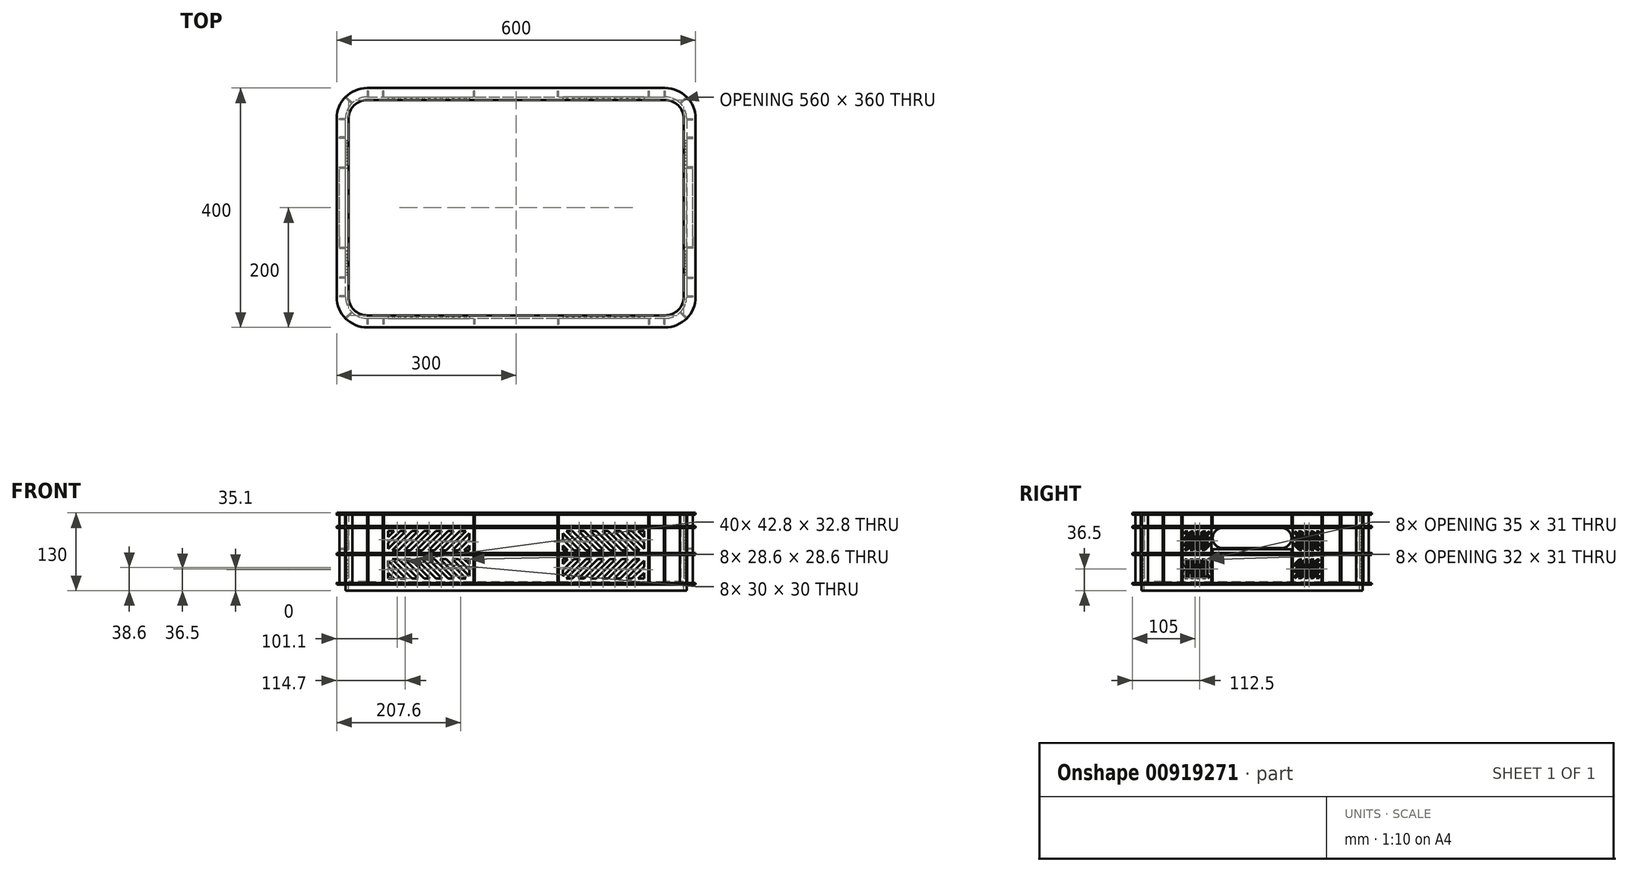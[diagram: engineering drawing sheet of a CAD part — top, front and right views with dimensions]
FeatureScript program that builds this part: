
annotation { "Feature Type Name" : "Feature", "Feature Type Description" : "" }
export const myFeature = defineFeature(function(context is Context, id is Id, definition is map)
    precondition{}
    {
        {
            var Q0;
            Q0=qCreatedBy(makeId("Top.planeOp"),FACE);
            var sketch = newSketch(context, id + "F0", { "sketchPlane" : qUnion([Q0])});
            skLineSegment(sketch, "E0.bottom", {"start": v(249, 185) * mm, "end": v(-249, 185) * mm});
            skLineSegment(sketch, "E0.top", {"start": v(249, -185) * mm, "end": v(-249, -185) * mm});
            skLineSegment(sketch, "E0.left", {"start": v(285, 149) * mm, "end": v(285, -149) * mm});
            skLineSegment(sketch, "E0.right", {"start": v(-285, 149) * mm, "end": v(-285, -149) * mm});
            skPoint(sketch, "E0.middle", {"position": v(0, 0) * mm});
            skPoint(sketch, "E1.visualSharp", {"position": v(-285, 185) * mm});
            skArc(sketch, "E1.filletArc", {"start": v(-249, 185) * mm, "mid": v(-274.46, 174.46) * mm, "end": v(-285, 149) * mm});
            skPoint(sketch, "E2.visualSharp", {"position": v(285, 185) * mm});
            skArc(sketch, "E2.filletArc", {"start": v(285, 149) * mm, "mid": v(274.46, 174.46) * mm, "end": v(249, 185) * mm});
            skPoint(sketch, "E3.visualSharp", {"position": v(285, -185) * mm});
            skArc(sketch, "E3.filletArc", {"start": v(249, -185) * mm, "mid": v(274.46, -174.46) * mm, "end": v(285, -149) * mm});
            skPoint(sketch, "E4.visualSharp", {"position": v(-285, -185) * mm});
            skArc(sketch, "E4.filletArc", {"start": v(-285, -149) * mm, "mid": v(-274.46, -174.46) * mm, "end": v(-249, -185) * mm});
            skSolve(sketch);
        }
        {
            var Q0;
            Q0 = qSketchRegion(id + "F0", true);
            extrude(context, id + "F1", {"entities" : qUnion([Q0]), "depth" : 120 * mm, "offsetDistance" : 25 * mm});
        }
        {
            var Q0;
            Q0=makeQuery(id+"F1.opExtrude","CAP_FACE",FACE,{"disambiguationData":[OSD([sQuery(id+"F0.wireOp",EDGE,"E0.bottom"),sQuery(id+"F0.wireOp",EDGE,"E0.top"),sQuery(id+"F0.wireOp",EDGE,"E0.left"),sQuery(id+"F0.wireOp",EDGE,"E0.right"),sQuery(id+"F0.wireOp",EDGE,"E1.filletArc"),sQuery(id+"F0.wireOp",EDGE,"E2.filletArc"),sQuery(id+"F0.wireOp",EDGE,"E3.filletArc"),sQuery(id+"F0.wireOp",EDGE,"E4.filletArc")])],"isStart":false});
            var sketch = newSketch(context, id + "F2", { "sketchPlane" : qUnion([Q0])});
            skArc(sketch, "E5.0", {"start": v(300, 149) * mm, "mid": v(285.06, 185.06) * mm, "end": v(249, 200) * mm});
            skLineSegment(sketch, "E5.1", {"start": v(300, 149) * mm, "end": v(300, -149) * mm});
            skLineSegment(sketch, "E5.2", {"start": v(249, 200) * mm, "end": v(-249, 200) * mm});
            skArc(sketch, "E5.3", {"start": v(249, -200) * mm, "mid": v(285.06, -185.06) * mm, "end": v(300, -149) * mm});
            skArc(sketch, "E5.4", {"start": v(-249, 200) * mm, "mid": v(-285.06, 185.06) * mm, "end": v(-300, 149) * mm});
            skLineSegment(sketch, "E5.5", {"start": v(-300, 149) * mm, "end": v(-300, -149) * mm});
            skArc(sketch, "E5.6", {"start": v(-300, -149) * mm, "mid": v(-285.06, -185.06) * mm, "end": v(-249, -200) * mm});
            skLineSegment(sketch, "E5.7", {"start": v(249, -200) * mm, "end": v(-249, -200) * mm});
            skSolve(sketch);
        }
        {
            var Q0;
            Q0 = qSketchRegion(id + "F2", true);
            extrude(context, id + "F3", {"entities" : qUnion([Q0]), "operationType" : NewBodyOperationType.ADD, "oppositeDirection" : true, "depth" : 3 * mm, "offsetDistance" : 25 * mm});
        }
        {
            var Q0;
            Q0=makeQuery(id+"F3.boolean.opBoolean","MERGE",FACE,{"derivedFrom":[makeQuery(id+"F1.opExtrude","CAP_FACE",FACE,{"disambiguationData":[OSD([sQuery(id+"F0.wireOp",EDGE,"E0.bottom"),sQuery(id+"F0.wireOp",EDGE,"E0.top"),sQuery(id+"F0.wireOp",EDGE,"E0.left"),sQuery(id+"F0.wireOp",EDGE,"E0.right"),sQuery(id+"F0.wireOp",EDGE,"E1.filletArc"),sQuery(id+"F0.wireOp",EDGE,"E2.filletArc"),sQuery(id+"F0.wireOp",EDGE,"E3.filletArc"),sQuery(id+"F0.wireOp",EDGE,"E4.filletArc")])],"isStart":false}),makeQuery(id+"F3.opExtrude","CAP_FACE",FACE,{"disambiguationData":[OSD([sQuery(id+"F2.wireOp",EDGE,"E5.0"),sQuery(id+"F2.wireOp",EDGE,"E5.1"),sQuery(id+"F2.wireOp",EDGE,"E5.2"),sQuery(id+"F2.wireOp",EDGE,"E5.3"),sQuery(id+"F2.wireOp",EDGE,"E5.4"),sQuery(id+"F2.wireOp",EDGE,"E5.5"),sQuery(id+"F2.wireOp",EDGE,"E5.6"),sQuery(id+"F2.wireOp",EDGE,"E5.7")])],"isStart":true})]});
            cPlane(context, id + "F4", {"entities" : qUnion([Q0]), "cplaneType" : CPlaneType.OFFSET, "offset" : 25 * mm, "oppositeDirection" : true, "width" : 150 * mm, "height" : 150 * mm});
        }
        {
            var Q0;
            Q0=qCreatedBy(id+"F4.planeOp",FACE);
            var sketch = newSketch(context, id + "F5", { "sketchPlane" : qUnion([Q0])});
            skLineSegment(sketch, "E6.0.0", {"start": v(249, -185) * mm, "end": v(-249, -185) * mm});
            skArc(sketch, "E6.0.1", {"start": v(-249, -185) * mm, "mid": v(-274.46, -174.46) * mm, "end": v(-285, -149) * mm});
            skLineSegment(sketch, "E6.0.2", {"start": v(-285, -149) * mm, "end": v(-285, 149) * mm});
            skArc(sketch, "E6.0.3", {"start": v(-285, 149) * mm, "mid": v(-274.46, 174.46) * mm, "end": v(-249, 185) * mm});
            skLineSegment(sketch, "E6.0.4", {"start": v(-249, 185) * mm, "end": v(249, 185) * mm});
            skArc(sketch, "E6.0.5", {"start": v(249, 185) * mm, "mid": v(274.46, 174.46) * mm, "end": v(285, 149) * mm});
            skLineSegment(sketch, "E6.0.6", {"start": v(285, 149) * mm, "end": v(285, -149) * mm});
            skArc(sketch, "E6.0.7", {"start": v(285, -149) * mm, "mid": v(274.46, -174.46) * mm, "end": v(249, -185) * mm});
            skLineSegment(sketch, "E7.0.0", {"start": v(249, -200) * mm, "end": v(-249, -200) * mm});
            skArc(sketch, "E7.0.1", {"start": v(-249, -200) * mm, "mid": v(-285.06, -185.06) * mm, "end": v(-300, -149) * mm});
            skLineSegment(sketch, "E7.0.2", {"start": v(-300, -149) * mm, "end": v(-300, 149) * mm});
            skArc(sketch, "E7.0.3", {"start": v(-300, 149) * mm, "mid": v(-285.06, 185.06) * mm, "end": v(-249, 200) * mm});
            skLineSegment(sketch, "E7.0.4", {"start": v(-249, 200) * mm, "end": v(249, 200) * mm});
            skArc(sketch, "E7.0.5", {"start": v(249, 200) * mm, "mid": v(285.06, 185.06) * mm, "end": v(300, 149) * mm});
            skLineSegment(sketch, "E7.0.6", {"start": v(300, 149) * mm, "end": v(300, -149) * mm});
            skArc(sketch, "E7.0.7", {"start": v(300, -149) * mm, "mid": v(285.06, -185.06) * mm, "end": v(249, -200) * mm});
            skSolve(sketch);
        }
        {
            var Q0;
            Q0 = qSketchRegion(id + "F5", true);
            extrude(context, id + "F6", {"entities" : qUnion([Q0]), "operationType" : NewBodyOperationType.ADD, "depth" : 3 * mm, "offsetDistance" : 25 * mm});
        }
        {
            var Q0;
            Q0=makeQuery(id+"F3.boolean.opBoolean","MERGE",FACE,{"derivedFrom":[makeQuery(id+"F1.opExtrude","CAP_FACE",FACE,{"disambiguationData":[OSD([sQuery(id+"F0.wireOp",EDGE,"E0.bottom"),sQuery(id+"F0.wireOp",EDGE,"E0.top"),sQuery(id+"F0.wireOp",EDGE,"E0.left"),sQuery(id+"F0.wireOp",EDGE,"E0.right"),sQuery(id+"F0.wireOp",EDGE,"E1.filletArc"),sQuery(id+"F0.wireOp",EDGE,"E2.filletArc"),sQuery(id+"F0.wireOp",EDGE,"E3.filletArc"),sQuery(id+"F0.wireOp",EDGE,"E4.filletArc")])],"isStart":false}),makeQuery(id+"F3.opExtrude","CAP_FACE",FACE,{"disambiguationData":[OSD([sQuery(id+"F2.wireOp",EDGE,"E5.0"),sQuery(id+"F2.wireOp",EDGE,"E5.1"),sQuery(id+"F2.wireOp",EDGE,"E5.2"),sQuery(id+"F2.wireOp",EDGE,"E5.3"),sQuery(id+"F2.wireOp",EDGE,"E5.4"),sQuery(id+"F2.wireOp",EDGE,"E5.5"),sQuery(id+"F2.wireOp",EDGE,"E5.6"),sQuery(id+"F2.wireOp",EDGE,"E5.7")])],"isStart":true})]});
            cPlane(context, id + "F7", {"entities" : qUnion([Q0]), "cplaneType" : CPlaneType.OFFSET, "offset" : 70 * mm, "oppositeDirection" : true, "width" : 150 * mm, "height" : 150 * mm});
        }
        {
            var Q0;
            Q0=qCreatedBy(id+"F7.planeOp",FACE);
            var sketch = newSketch(context, id + "F8", { "sketchPlane" : qUnion([Q0])});
            skLineSegment(sketch, "E8.0.0", {"start": v(249, -185) * mm, "end": v(-249, -185) * mm});
            skArc(sketch, "E8.0.1", {"start": v(-249, -185) * mm, "mid": v(-274.46, -174.46) * mm, "end": v(-285, -149) * mm});
            skLineSegment(sketch, "E8.0.2", {"start": v(-285, -149) * mm, "end": v(-285, 149) * mm});
            skArc(sketch, "E8.0.3", {"start": v(-285, 149) * mm, "mid": v(-274.46, 174.46) * mm, "end": v(-249, 185) * mm});
            skLineSegment(sketch, "E8.0.4", {"start": v(-249, 185) * mm, "end": v(249, 185) * mm});
            skArc(sketch, "E8.0.5", {"start": v(249, 185) * mm, "mid": v(274.46, 174.46) * mm, "end": v(285, 149) * mm});
            skLineSegment(sketch, "E8.0.6", {"start": v(285, 149) * mm, "end": v(285, -149) * mm});
            skArc(sketch, "E8.0.7", {"start": v(285, -149) * mm, "mid": v(274.46, -174.46) * mm, "end": v(249, -185) * mm});
            skArc(sketch, "E9.0.0", {"start": v(300, -149) * mm, "mid": v(285.06, -185.06) * mm, "end": v(249, -200) * mm});
            skLineSegment(sketch, "E9.0.1", {"start": v(249, -200) * mm, "end": v(-249, -200) * mm});
            skArc(sketch, "E9.0.2", {"start": v(-249, -200) * mm, "mid": v(-285.06, -185.06) * mm, "end": v(-300, -149) * mm});
            skLineSegment(sketch, "E9.0.3", {"start": v(-300, -149) * mm, "end": v(-300, 149) * mm});
            skArc(sketch, "E9.0.4", {"start": v(-300, 149) * mm, "mid": v(-285.06, 185.06) * mm, "end": v(-249, 200) * mm});
            skLineSegment(sketch, "E9.0.5", {"start": v(-249, 200) * mm, "end": v(249, 200) * mm});
            skArc(sketch, "E9.0.6", {"start": v(249, 200) * mm, "mid": v(285.06, 185.06) * mm, "end": v(300, 149) * mm});
            skLineSegment(sketch, "E9.0.7", {"start": v(300, 149) * mm, "end": v(300, -149) * mm});
            skSolve(sketch);
        }
        {
            var Q0;
            Q0 = qSketchRegion(id + "F8", true);
            extrude(context, id + "F9", {"entities" : qUnion([Q0]), "operationType" : NewBodyOperationType.ADD, "depth" : 3 * mm, "offsetDistance" : 25 * mm});
        }
        {
            var Q0;
            Q0=makeQuery(id+"F1.opExtrude","CAP_FACE",FACE,{"disambiguationData":[OSD([sQuery(id+"F0.wireOp",EDGE,"E0.bottom"),sQuery(id+"F0.wireOp",EDGE,"E0.top"),sQuery(id+"F0.wireOp",EDGE,"E0.left"),sQuery(id+"F0.wireOp",EDGE,"E0.right"),sQuery(id+"F0.wireOp",EDGE,"E1.filletArc"),sQuery(id+"F0.wireOp",EDGE,"E2.filletArc"),sQuery(id+"F0.wireOp",EDGE,"E3.filletArc"),sQuery(id+"F0.wireOp",EDGE,"E4.filletArc")])],"isStart":true});
            var sketch = newSketch(context, id + "F10", { "sketchPlane" : qUnion([Q0])});
            skLineSegment(sketch, "E10.0.0", {"start": v(249, 185) * mm, "end": v(-249, 185) * mm});
            skArc(sketch, "E10.0.1", {"start": v(-249, 185) * mm, "mid": v(-274.46, 174.46) * mm, "end": v(-285, 149) * mm});
            skLineSegment(sketch, "E10.0.2", {"start": v(-285, 149) * mm, "end": v(-285, -149) * mm});
            skArc(sketch, "E10.0.3", {"start": v(-285, -149) * mm, "mid": v(-274.46, -174.46) * mm, "end": v(-249, -185) * mm});
            skLineSegment(sketch, "E10.0.4", {"start": v(-249, -185) * mm, "end": v(249, -185) * mm});
            skArc(sketch, "E10.0.5", {"start": v(249, -185) * mm, "mid": v(274.46, -174.46) * mm, "end": v(285, -149) * mm});
            skLineSegment(sketch, "E10.0.6", {"start": v(285, -149) * mm, "end": v(285, 149) * mm});
            skArc(sketch, "E10.0.7", {"start": v(285, 149) * mm, "mid": v(274.46, 174.46) * mm, "end": v(249, 185) * mm});
            skLineSegment(sketch, "E11.0.0", {"start": v(300, -149) * mm, "end": v(300, 149) * mm});
            skArc(sketch, "E11.0.1", {"start": v(300, 149) * mm, "mid": v(285.06, 185.06) * mm, "end": v(249, 200) * mm});
            skLineSegment(sketch, "E11.0.2", {"start": v(249, 200) * mm, "end": v(-249, 200) * mm});
            skArc(sketch, "E11.0.3", {"start": v(-249, 200) * mm, "mid": v(-285.06, 185.06) * mm, "end": v(-300, 149) * mm});
            skLineSegment(sketch, "E11.0.4", {"start": v(-300, 149) * mm, "end": v(-300, -149) * mm});
            skArc(sketch, "E11.0.5", {"start": v(-300, -149) * mm, "mid": v(-285.06, -185.06) * mm, "end": v(-249, -200) * mm});
            skLineSegment(sketch, "E11.0.6", {"start": v(-249, -200) * mm, "end": v(249, -200) * mm});
            skArc(sketch, "E11.0.7", {"start": v(249, -200) * mm, "mid": v(285.06, -185.06) * mm, "end": v(300, -149) * mm});
            skSolve(sketch);
        }
        {
            var Q0;
            Q0 = qSketchRegion(id + "F10", true);
            extrude(context, id + "F11", {"entities" : qUnion([Q0]), "operationType" : NewBodyOperationType.ADD, "oppositeDirection" : true, "depth" : 3 * mm, "offsetDistance" : 25 * mm});
        }
        {
            var Q0;
            Q0=makeQuery(id+"F3.boolean.opBoolean","MERGE",FACE,{"derivedFrom":[makeQuery(id+"F1.opExtrude","CAP_FACE",FACE,{"disambiguationData":[OSD([sQuery(id+"F0.wireOp",EDGE,"E0.bottom"),sQuery(id+"F0.wireOp",EDGE,"E0.top"),sQuery(id+"F0.wireOp",EDGE,"E0.left"),sQuery(id+"F0.wireOp",EDGE,"E0.right"),sQuery(id+"F0.wireOp",EDGE,"E1.filletArc"),sQuery(id+"F0.wireOp",EDGE,"E2.filletArc"),sQuery(id+"F0.wireOp",EDGE,"E3.filletArc"),sQuery(id+"F0.wireOp",EDGE,"E4.filletArc")])],"isStart":false}),makeQuery(id+"F3.opExtrude","CAP_FACE",FACE,{"disambiguationData":[OSD([sQuery(id+"F2.wireOp",EDGE,"E5.0"),sQuery(id+"F2.wireOp",EDGE,"E5.1"),sQuery(id+"F2.wireOp",EDGE,"E5.2"),sQuery(id+"F2.wireOp",EDGE,"E5.3"),sQuery(id+"F2.wireOp",EDGE,"E5.4"),sQuery(id+"F2.wireOp",EDGE,"E5.5"),sQuery(id+"F2.wireOp",EDGE,"E5.6"),sQuery(id+"F2.wireOp",EDGE,"E5.7")])],"isStart":true})]});
            shell(context, id + "F12", {"entities" : qUnion([Q0]), "thickness" : 5 * mm});
        }
        {
            var Q0;
            Q0=makeQuery(id+"F11.boolean.opBoolean","MERGE",FACE,{"derivedFrom":[makeQuery(id+"F1.opExtrude","CAP_FACE",FACE,{"disambiguationData":[OSD([sQuery(id+"F0.wireOp",EDGE,"E0.bottom"),sQuery(id+"F0.wireOp",EDGE,"E0.top"),sQuery(id+"F0.wireOp",EDGE,"E0.left"),sQuery(id+"F0.wireOp",EDGE,"E0.right"),sQuery(id+"F0.wireOp",EDGE,"E1.filletArc"),sQuery(id+"F0.wireOp",EDGE,"E2.filletArc"),sQuery(id+"F0.wireOp",EDGE,"E3.filletArc"),sQuery(id+"F0.wireOp",EDGE,"E4.filletArc")])],"isStart":true}),makeQuery(id+"F11.opExtrude","CAP_FACE",FACE,{"disambiguationData":[OSD([sQuery(id+"F10.wireOp",EDGE,"E10.0.0"),sQuery(id+"F10.wireOp",EDGE,"E10.0.1"),sQuery(id+"F10.wireOp",EDGE,"E10.0.2"),sQuery(id+"F10.wireOp",EDGE,"E10.0.3"),sQuery(id+"F10.wireOp",EDGE,"E10.0.4"),sQuery(id+"F10.wireOp",EDGE,"E10.0.5"),sQuery(id+"F10.wireOp",EDGE,"E10.0.6"),sQuery(id+"F10.wireOp",EDGE,"E10.0.7"),sQuery(id+"F10.wireOp",EDGE,"E11.0.0"),sQuery(id+"F10.wireOp",EDGE,"E11.0.1"),sQuery(id+"F10.wireOp",EDGE,"E11.0.2"),sQuery(id+"F10.wireOp",EDGE,"E11.0.3"),sQuery(id+"F10.wireOp",EDGE,"E11.0.4"),sQuery(id+"F10.wireOp",EDGE,"E11.0.5"),sQuery(id+"F10.wireOp",EDGE,"E11.0.6"),sQuery(id+"F10.wireOp",EDGE,"E11.0.7")])],"isStart":true})]});
            var sketch = newSketch(context, id + "F13", { "sketchPlane" : qUnion([Q0])});
            skLineSegment(sketch, "E12.0", {"start": v(249, 185) * mm, "end": v(-249, 185) * mm});
            skArc(sketch, "E12.1", {"start": v(285, 149) * mm, "mid": v(274.46, 174.46) * mm, "end": v(249, 185) * mm});
            skArc(sketch, "E12.2", {"start": v(-249, 185) * mm, "mid": v(-274.46, 174.46) * mm, "end": v(-285, 149) * mm});
            skLineSegment(sketch, "E12.3", {"start": v(285, -149) * mm, "end": v(285, 149) * mm});
            skLineSegment(sketch, "E12.4", {"start": v(-285, 149) * mm, "end": v(-285, -149) * mm});
            skArc(sketch, "E12.5", {"start": v(-285, -149) * mm, "mid": v(-274.46, -174.46) * mm, "end": v(-249, -185) * mm});
            skLineSegment(sketch, "E12.6", {"start": v(-249, -185) * mm, "end": v(249, -185) * mm});
            skArc(sketch, "E12.7", {"start": v(249, -185) * mm, "mid": v(274.46, -174.46) * mm, "end": v(285, -149) * mm});
            skArc(sketch, "E13.0", {"start": v(280, 149) * mm, "mid": v(270.92, 170.92) * mm, "end": v(249, 180) * mm});
            skLineSegment(sketch, "E13.1", {"start": v(280, -149) * mm, "end": v(280, 149) * mm});
            skLineSegment(sketch, "E13.2", {"start": v(249, 180) * mm, "end": v(-249, 180) * mm});
            skArc(sketch, "E13.3", {"start": v(249, -180) * mm, "mid": v(270.92, -170.92) * mm, "end": v(280, -149) * mm});
            skArc(sketch, "E13.4", {"start": v(-249, 180) * mm, "mid": v(-270.92, 170.92) * mm, "end": v(-280, 149) * mm});
            skLineSegment(sketch, "E13.5", {"start": v(-280, 149) * mm, "end": v(-280, -149) * mm});
            skArc(sketch, "E13.6", {"start": v(-280, -149) * mm, "mid": v(-270.92, -170.92) * mm, "end": v(-249, -180) * mm});
            skLineSegment(sketch, "E13.7", {"start": v(-249, -180) * mm, "end": v(249, -180) * mm});
            skSolve(sketch);
        }
        {
            var Q0;
            Q0 = qSketchRegion(id + "F13", true);
            extrude(context, id + "F14", {"entities" : qUnion([Q0]), "operationType" : NewBodyOperationType.ADD, "depth" : 10 * mm, "offsetDistance" : 25 * mm});
        }
        {
            var Q0;
            Q0=makeQuery(id+"F14.boolean.opBoolean","SPLIT",FACE,{"disambiguationData":[TD([makeQuery(id+"F14.opExtrude","SWEPT_FACE",FACE,{"disambiguationData":[OSD([sQuery(id+"F13.wireOp",EDGE,"E13.0")])]})])],"derivedFrom":makeQuery(id+"F11.boolean.opBoolean","MERGE",FACE,{"derivedFrom":[makeQuery(id+"F1.opExtrude","CAP_FACE",FACE,{"disambiguationData":[OSD([sQuery(id+"F0.wireOp",EDGE,"E0.bottom"),sQuery(id+"F0.wireOp",EDGE,"E0.top"),sQuery(id+"F0.wireOp",EDGE,"E0.left"),sQuery(id+"F0.wireOp",EDGE,"E0.right"),sQuery(id+"F0.wireOp",EDGE,"E1.filletArc"),sQuery(id+"F0.wireOp",EDGE,"E2.filletArc"),sQuery(id+"F0.wireOp",EDGE,"E3.filletArc"),sQuery(id+"F0.wireOp",EDGE,"E4.filletArc")])],"isStart":true}),makeQuery(id+"F11.opExtrude","CAP_FACE",FACE,{"disambiguationData":[OSD([sQuery(id+"F10.wireOp",EDGE,"E10.0.0"),sQuery(id+"F10.wireOp",EDGE,"E10.0.1"),sQuery(id+"F10.wireOp",EDGE,"E10.0.2"),sQuery(id+"F10.wireOp",EDGE,"E10.0.3"),sQuery(id+"F10.wireOp",EDGE,"E10.0.4"),sQuery(id+"F10.wireOp",EDGE,"E10.0.5"),sQuery(id+"F10.wireOp",EDGE,"E10.0.6"),sQuery(id+"F10.wireOp",EDGE,"E10.0.7"),sQuery(id+"F10.wireOp",EDGE,"E11.0.0"),sQuery(id+"F10.wireOp",EDGE,"E11.0.1"),sQuery(id+"F10.wireOp",EDGE,"E11.0.2"),sQuery(id+"F10.wireOp",EDGE,"E11.0.3"),sQuery(id+"F10.wireOp",EDGE,"E11.0.4"),sQuery(id+"F10.wireOp",EDGE,"E11.0.5"),sQuery(id+"F10.wireOp",EDGE,"E11.0.6"),sQuery(id+"F10.wireOp",EDGE,"E11.0.7")])],"isStart":true})]})});
            var sketch = newSketch(context, id + "F15", { "sketchPlane" : qUnion([Q0])});
            skLineSegment(sketch, "E14.bottom", {"start": v(-249, 185) * mm, "end": v(-247, 185) * mm});
            skLineSegment(sketch, "E14.top", {"start": v(-249, 195) * mm, "end": v(-247, 195) * mm});
            skLineSegment(sketch, "E14.left", {"start": v(-249, 185) * mm, "end": v(-249, 195) * mm});
            skLineSegment(sketch, "E14.right", {"start": v(-247, 185) * mm, "end": v(-247, 195) * mm});
            skLineSegment(sketch, "E15.bottom", {"start": v(-71, 195) * mm, "end": v(-69, 195) * mm});
            skLineSegment(sketch, "E15.top", {"start": v(-71, 185) * mm, "end": v(-69, 185) * mm});
            skLineSegment(sketch, "E15.left", {"start": v(-71, 195) * mm, "end": v(-71, 185) * mm});
            skLineSegment(sketch, "E15.right", {"start": v(-69, 195) * mm, "end": v(-69, 185) * mm});
            skLineSegment(sketch, "E16.bottom", {"start": v(-223, 195) * mm, "end": v(-221, 195) * mm});
            skLineSegment(sketch, "E16.top", {"start": v(-223, 185) * mm, "end": v(-221, 185) * mm});
            skLineSegment(sketch, "E16.left", {"start": v(-223, 195) * mm, "end": v(-223, 185) * mm});
            skLineSegment(sketch, "E16.right", {"start": v(-221, 195) * mm, "end": v(-221, 185) * mm});
            skLineSegment(sketch, "E17.bottom", {"start": v(-285, 68) * mm, "end": v(-295, 68) * mm});
            skLineSegment(sketch, "E17.top", {"start": v(-285, 66) * mm, "end": v(-295, 66) * mm});
            skLineSegment(sketch, "E17.left", {"start": v(-285, 68) * mm, "end": v(-285, 66) * mm});
            skLineSegment(sketch, "E17.right", {"start": v(-295, 68) * mm, "end": v(-295, 66) * mm});
            skLineSegment(sketch, "E18.bottom", {"start": v(-295, 149) * mm, "end": v(-285, 149) * mm});
            skLineSegment(sketch, "E18.top", {"start": v(-295, 147) * mm, "end": v(-285, 147) * mm});
            skLineSegment(sketch, "E18.left", {"start": v(-295, 149) * mm, "end": v(-295, 147) * mm});
            skLineSegment(sketch, "E18.right", {"start": v(-285, 149) * mm, "end": v(-285, 147) * mm});
            skLineSegment(sketch, "E19.bottom", {"start": v(-295, 118) * mm, "end": v(-285, 118) * mm});
            skLineSegment(sketch, "E19.top", {"start": v(-295, 116) * mm, "end": v(-285, 116) * mm});
            skLineSegment(sketch, "E19.left", {"start": v(-295, 118) * mm, "end": v(-295, 116) * mm});
            skLineSegment(sketch, "E19.right", {"start": v(-285, 118) * mm, "end": v(-285, 116) * mm});
            skSolve(sketch);
        }
        {
            var Q0;
            Q0 = qSketchRegion(id + "F15", true);
            var Q1;
            Q1=makeQuery(id+"F3.opExtrude","CAP_FACE",FACE,{"disambiguationData":[OSD([sQuery(id+"F2.wireOp",EDGE,"E5.0"),sQuery(id+"F2.wireOp",EDGE,"E5.1"),sQuery(id+"F2.wireOp",EDGE,"E5.2"),sQuery(id+"F2.wireOp",EDGE,"E5.3"),sQuery(id+"F2.wireOp",EDGE,"E5.4"),sQuery(id+"F2.wireOp",EDGE,"E5.5"),sQuery(id+"F2.wireOp",EDGE,"E5.6"),sQuery(id+"F2.wireOp",EDGE,"E5.7")])],"isStart":false});
            extrude(context, id + "F16", {"entities" : qUnion([Q0]), "operationType" : NewBodyOperationType.ADD, "endBound" : BoundingType.UP_TO_SURFACE, "oppositeDirection" : true, "depth" : 25 * mm, "endBoundEntityFace" : qUnion([Q1]), "offsetDistance" : 25 * mm});
        }
        {
            var Q0;
            Q0=makeQuery(id+"F14.boolean.opBoolean","SPLIT",FACE,{"disambiguationData":[TD([makeQuery(id+"F14.opExtrude","SWEPT_FACE",FACE,{"disambiguationData":[OSD([sQuery(id+"F13.wireOp",EDGE,"E13.0")])]})])],"derivedFrom":makeQuery(id+"F11.boolean.opBoolean","MERGE",FACE,{"derivedFrom":[makeQuery(id+"F1.opExtrude","CAP_FACE",FACE,{"disambiguationData":[OSD([sQuery(id+"F0.wireOp",EDGE,"E0.bottom"),sQuery(id+"F0.wireOp",EDGE,"E0.top"),sQuery(id+"F0.wireOp",EDGE,"E0.left"),sQuery(id+"F0.wireOp",EDGE,"E0.right"),sQuery(id+"F0.wireOp",EDGE,"E1.filletArc"),sQuery(id+"F0.wireOp",EDGE,"E2.filletArc"),sQuery(id+"F0.wireOp",EDGE,"E3.filletArc"),sQuery(id+"F0.wireOp",EDGE,"E4.filletArc")])],"isStart":true}),makeQuery(id+"F11.opExtrude","CAP_FACE",FACE,{"disambiguationData":[OSD([sQuery(id+"F10.wireOp",EDGE,"E10.0.0"),sQuery(id+"F10.wireOp",EDGE,"E10.0.1"),sQuery(id+"F10.wireOp",EDGE,"E10.0.2"),sQuery(id+"F10.wireOp",EDGE,"E10.0.3"),sQuery(id+"F10.wireOp",EDGE,"E10.0.4"),sQuery(id+"F10.wireOp",EDGE,"E10.0.5"),sQuery(id+"F10.wireOp",EDGE,"E10.0.6"),sQuery(id+"F10.wireOp",EDGE,"E10.0.7"),sQuery(id+"F10.wireOp",EDGE,"E11.0.0"),sQuery(id+"F10.wireOp",EDGE,"E11.0.1"),sQuery(id+"F10.wireOp",EDGE,"E11.0.2"),sQuery(id+"F10.wireOp",EDGE,"E11.0.3"),sQuery(id+"F10.wireOp",EDGE,"E11.0.4"),sQuery(id+"F10.wireOp",EDGE,"E11.0.5"),sQuery(id+"F10.wireOp",EDGE,"E11.0.6"),sQuery(id+"F10.wireOp",EDGE,"E11.0.7")])],"isStart":true})]})});
            var sketch = newSketch(context, id + "F17", { "sketchPlane" : qUnion([Q0])});
            skLineSegment(sketch, "E20", {"start": v(-285.06, 185.06) * mm, "end": v(-270.92, 170.92) * mm, "construction": true});
            skArc(sketch, "E21.0", {"start": v(-273.74, 175.15) * mm, "mid": v(-274.46, 174.46) * mm, "end": v(-275.15, 173.74) * mm});
            skArc(sketch, "E22.0", {"start": v(-284.35, 185.76) * mm, "mid": v(-285.06, 185.06) * mm, "end": v(-285.76, 184.35) * mm});
            skLineSegment(sketch, "E23.0", {"start": v(-285.76, 184.35) * mm, "end": v(-275.15, 173.74) * mm});
            skLineSegment(sketch, "E24.0", {"start": v(-284.35, 185.76) * mm, "end": v(-273.74, 175.15) * mm});
            skPoint(sketch, "E25.orphan", {"position": v(-249, 185) * mm});
            skPoint(sketch, "E26.orphan", {"position": v(-249, 200) * mm});
            skPoint(sketch, "E27.orphan", {"position": v(-300, 149) * mm});
            skPoint(sketch, "E28.orphan", {"position": v(-285, 149) * mm});
            skSolve(sketch);
        }
        {
            var Q0;
            Q0 = qSketchRegion(id + "F17", true);
            var Q1;
            Q1=makeQuery(id+"F3.opExtrude","CAP_FACE",FACE,{"disambiguationData":[OSD([sQuery(id+"F2.wireOp",EDGE,"E5.0"),sQuery(id+"F2.wireOp",EDGE,"E5.1"),sQuery(id+"F2.wireOp",EDGE,"E5.2"),sQuery(id+"F2.wireOp",EDGE,"E5.3"),sQuery(id+"F2.wireOp",EDGE,"E5.4"),sQuery(id+"F2.wireOp",EDGE,"E5.5"),sQuery(id+"F2.wireOp",EDGE,"E5.6"),sQuery(id+"F2.wireOp",EDGE,"E5.7")])],"isStart":false});
            extrude(context, id + "F18", {"entities" : qUnion([Q0]), "operationType" : NewBodyOperationType.ADD, "endBound" : BoundingType.UP_TO_SURFACE, "oppositeDirection" : true, "depth" : 25 * mm, "endBoundEntityFace" : qUnion([Q1]), "offsetDistance" : 25 * mm});
        }
        {
            var Q0;
            Q0=makeQuery(id+"F1.opExtrude","SWEPT_BODY",BODY,{"disambiguationData":[OSD([sQuery(id+"F0.wireOp",EDGE,"E0.bottom"),sQuery(id+"F0.wireOp",EDGE,"E0.top"),sQuery(id+"F0.wireOp",EDGE,"E0.left"),sQuery(id+"F0.wireOp",EDGE,"E0.right"),sQuery(id+"F0.wireOp",EDGE,"E1.filletArc"),sQuery(id+"F0.wireOp",EDGE,"E2.filletArc"),sQuery(id+"F0.wireOp",EDGE,"E3.filletArc"),sQuery(id+"F0.wireOp",EDGE,"E4.filletArc")])]});
            var Q1;
            Q1=qCreatedBy(makeId("Right.planeOp"),FACE);
            mirror(context, id + "F19", {"operationType" : NewBodyOperationType.ADD, "entities" : qUnion([Q0]), "mirrorPlane" : qUnion([Q1])});
        }
        {
            var Q0;
            Q0=makeQuery(id+"F1.opExtrude","SWEPT_BODY",BODY,{"disambiguationData":[OSD([sQuery(id+"F0.wireOp",EDGE,"E0.bottom"),sQuery(id+"F0.wireOp",EDGE,"E0.top"),sQuery(id+"F0.wireOp",EDGE,"E0.left"),sQuery(id+"F0.wireOp",EDGE,"E0.right"),sQuery(id+"F0.wireOp",EDGE,"E1.filletArc"),sQuery(id+"F0.wireOp",EDGE,"E2.filletArc"),sQuery(id+"F0.wireOp",EDGE,"E3.filletArc"),sQuery(id+"F0.wireOp",EDGE,"E4.filletArc")])]});
            var Q1;
            Q1=qCreatedBy(makeId("Right.planeOp"),FACE);
            mirror(context, id + "F20", {"operationType" : NewBodyOperationType.ADD, "entities" : qUnion([Q0]), "mirrorPlane" : qUnion([Q1])});
        }
        {
            var Q0;
            Q0=makeQuery(id+"F1.opExtrude","SWEPT_BODY",BODY,{"disambiguationData":[OSD([sQuery(id+"F0.wireOp",EDGE,"E0.bottom"),sQuery(id+"F0.wireOp",EDGE,"E0.top"),sQuery(id+"F0.wireOp",EDGE,"E0.left"),sQuery(id+"F0.wireOp",EDGE,"E0.right"),sQuery(id+"F0.wireOp",EDGE,"E1.filletArc"),sQuery(id+"F0.wireOp",EDGE,"E2.filletArc"),sQuery(id+"F0.wireOp",EDGE,"E3.filletArc"),sQuery(id+"F0.wireOp",EDGE,"E4.filletArc")])]});
            var Q1;
            Q1=qCreatedBy(makeId("Front.planeOp"),FACE);
            mirror(context, id + "F21", {"operationType" : NewBodyOperationType.ADD, "entities" : qUnion([Q0]), "mirrorPlane" : qUnion([Q1])});
        }
        {
            var Q0;
            {var subQ1=sQuery(id+"F0.wireOp",EDGE,"E4.filletArc");var subQ2=sQuery(id+"F0.wireOp",EDGE,"E3.filletArc");var subQ3=sQuery(id+"F0.wireOp",EDGE,"E0.top");var subQ4=makeQuery(id+"F1.opExtrude","CAP_FACE",FACE,{"disambiguationData":[OSD([sQuery(id+"F0.wireOp",EDGE,"E0.bottom"),subQ3,sQuery(id+"F0.wireOp",EDGE,"E0.left"),sQuery(id+"F0.wireOp",EDGE,"E0.right"),sQuery(id+"F0.wireOp",EDGE,"E1.filletArc"),sQuery(id+"F0.wireOp",EDGE,"E2.filletArc"),subQ2,subQ1])],"isStart":true});Q0=makeQuery(id+"F16.boolean.opBoolean","SPLIT",FACE,{"disambiguationData":[TD([makeQuery(id+"F16.opExtrude","SWEPT_FACE",FACE,{"disambiguationData":[OSD([sQuery(id+"F15.wireOp",EDGE,"E15.left")])]})])],"derivedFrom":makeQuery(id+"F9.boolean.opBoolean","SPLIT",FACE,{"disambiguationData":[TD([subQ4])],"derivedFrom":makeQuery(id+"F6.boolean.opBoolean","SPLIT",FACE,{"disambiguationData":[TD([subQ4])],"derivedFrom":makeQuery(id+"F1.opExtrude","SWEPT_FACE",FACE,{"disambiguationData":[OSD([subQ3])]})})})});}
            var sketch = newSketch(context, id + "F22", { "sketchPlane" : qUnion([Q0])});
            skLineSegment(sketch, "E29.bottom", {"start": v(-206.7, 42.9) * mm, "end": v(-196.7, 42.9) * mm});
            skLineSegment(sketch, "E29.top", {"start": v(-213.9, 10.1) * mm, "end": v(-203.9, 10.1) * mm});
            skLineSegment(sketch, "E29.left", {"start": v(-213.9, 40.1) * mm, "end": v(-213.9, 30.1) * mm});
            skLineSegment(sketch, "E29.right", {"start": v(-78.1, 42.9) * mm, "end": v(-78.1, 34.3) * mm});
            skLineSegment(sketch, "E30", {"start": v(-213.9, 20.1) * mm, "end": v(-203.9, 10.1) * mm});
            skLineSegment(sketch, "E31.1.0.0", {"start": v(-213.9, 30.1) * mm, "end": v(-193.9, 10.1) * mm});
            skLineSegment(sketch, "E31.2.0.0", {"start": v(-213.9, 40.1) * mm, "end": v(-183.9, 10.1) * mm});
            skLineSegment(sketch, "E31.3.0.0", {"start": v(-206.7, 42.9) * mm, "end": v(-173.9, 10.1) * mm});
            skLineSegment(sketch, "E31.4.0.0", {"start": v(-196.7, 42.9) * mm, "end": v(-163.9, 10.1) * mm});
            skLineSegment(sketch, "E31.5.0.0", {"start": v(-186.7, 42.9) * mm, "end": v(-153.9, 10.1) * mm});
            skLineSegment(sketch, "E31.6.0.0", {"start": v(-176.7, 42.9) * mm, "end": v(-143.9, 10.1) * mm});
            skLineSegment(sketch, "E31.7.0.0", {"start": v(-166.7, 42.9) * mm, "end": v(-133.9, 10.1) * mm});
            skLineSegment(sketch, "E31.8.0.0", {"start": v(-156.7, 42.9) * mm, "end": v(-123.9, 10.1) * mm});
            skLineSegment(sketch, "E31.9.0.0", {"start": v(-146.7, 42.9) * mm, "end": v(-113.9, 10.1) * mm});
            skLineSegment(sketch, "E31.10.0.0", {"start": v(-136.7, 42.9) * mm, "end": v(-103.9, 10.1) * mm});
            skLineSegment(sketch, "E31.11.0.0", {"start": v(-126.7, 42.9) * mm, "end": v(-93.9, 10.1) * mm});
            skLineSegment(sketch, "E31.12.0.0", {"start": v(-116.7, 42.9) * mm, "end": v(-83.9, 10.1) * mm});
            skLineSegment(sketch, "E31.13.0.0", {"start": v(-106.7, 42.9) * mm, "end": v(-78.1, 14.3) * mm});
            skLineSegment(sketch, "E31.14.0.0", {"start": v(-96.7, 42.9) * mm, "end": v(-78.1, 24.3) * mm});
            skLineSegment(sketch, "E31.15.0.0", {"start": v(-86.7, 42.9) * mm, "end": v(-78.1, 34.3) * mm});
            skPoint(sketch, "E32.orphan", {"position": v(-203.9, 20.1) * mm});
            skPoint(sketch, "E33.orphan", {"position": v(-193.9, 20.1) * mm});
            skPoint(sketch, "E34.orphan", {"position": v(-183.9, 20.1) * mm});
            skPoint(sketch, "E35.orphan", {"position": v(-173.9, 20.1) * mm});
            skPoint(sketch, "E36.orphan", {"position": v(-163.9, 20.1) * mm});
            skPoint(sketch, "E37.orphan", {"position": v(-153.9, 20.1) * mm});
            skPoint(sketch, "E38.orphan", {"position": v(-143.9, 20.1) * mm});
            skPoint(sketch, "E39.orphan", {"position": v(-133.9, 20.1) * mm});
            skPoint(sketch, "E40.orphan", {"position": v(-123.9, 20.1) * mm});
            skPoint(sketch, "E41.orphan", {"position": v(-113.9, 20.1) * mm});
            skPoint(sketch, "E42.orphan", {"position": v(-103.9, 20.1) * mm});
            skPoint(sketch, "E43.orphan", {"position": v(-93.9, 20.1) * mm});
            skPoint(sketch, "E44.orphan", {"position": v(-83.9, 20.1) * mm});
            skPoint(sketch, "E45.orphan", {"position": v(-73.9, 20.1) * mm});
            skPoint(sketch, "E46.orphan", {"position": v(-63.9, 20.1) * mm});
            skPoint(sketch, "E47.orphan", {"position": v(-53.9, 10.1) * mm});
            skPoint(sketch, "E48.orphan", {"position": v(-63.9, 10.1) * mm});
            skPoint(sketch, "E49.orphan", {"position": v(-73.9, 10.1) * mm});
            skLineSegment(sketch, "E50.trimOffspring", {"start": v(-213.9, 20.1) * mm, "end": v(-213.9, 10.1) * mm});
            skLineSegment(sketch, "E51.trimOffspring", {"start": v(-173.9, 10.1) * mm, "end": v(-163.9, 10.1) * mm});
            skLineSegment(sketch, "E52.trimOffspring", {"start": v(-153.9, 10.1) * mm, "end": v(-143.9, 10.1) * mm});
            skLineSegment(sketch, "E53.trimOffspring", {"start": v(-133.9, 10.1) * mm, "end": v(-123.9, 10.1) * mm});
            skLineSegment(sketch, "E54.trimOffspring", {"start": v(-113.9, 10.1) * mm, "end": v(-103.9, 10.1) * mm});
            skLineSegment(sketch, "E55.trimOffspring", {"start": v(-93.9, 10.1) * mm, "end": v(-83.9, 10.1) * mm});
            skLineSegment(sketch, "E56.trimOffspring", {"start": v(-78.1, 24.3) * mm, "end": v(-78.1, 14.3) * mm});
            skLineSegment(sketch, "E57.trimOffspring", {"start": v(-86.7, 42.9) * mm, "end": v(-78.1, 42.9) * mm});
            skLineSegment(sketch, "E58.trimOffspring", {"start": v(-106.7, 42.9) * mm, "end": v(-96.7, 42.9) * mm});
            skLineSegment(sketch, "E59.trimOffspring", {"start": v(-126.7, 42.9) * mm, "end": v(-116.7, 42.9) * mm});
            skLineSegment(sketch, "E60.trimOffspring", {"start": v(-146.7, 42.9) * mm, "end": v(-136.7, 42.9) * mm});
            skLineSegment(sketch, "E61.trimOffspring", {"start": v(-166.7, 42.9) * mm, "end": v(-156.7, 42.9) * mm});
            skLineSegment(sketch, "E62.trimOffspring", {"start": v(-186.7, 42.9) * mm, "end": v(-176.7, 42.9) * mm});
            skLineSegment(sketch, "E63.trimOffspring", {"start": v(-193.9, 10.1) * mm, "end": v(-183.9, 10.1) * mm});
            skLineSegment(sketch, "E64", {"start": v(-221, 50) * mm, "end": v(-71, 50) * mm, "construction": true});
            skLineSegment(sketch, "E65.MirrorCS", {"start": v(-213.9, 59.9) * mm, "end": v(-213.9, 69.9) * mm});
            skLineSegment(sketch, "E66.MirrorCS", {"start": v(-213.9, 59.9) * mm, "end": v(-183.9, 89.9) * mm});
            skPoint(sketch, "E67.MirrorP", {"position": v(-83.9, 79.9) * mm});
            skPoint(sketch, "E68.MirrorP", {"position": v(-143.9, 79.9) * mm});
            skPoint(sketch, "E69.MirrorP", {"position": v(-173.9, 79.9) * mm});
            skLineSegment(sketch, "E70.MirrorCS", {"start": v(-186.7, 57.1) * mm, "end": v(-153.9, 89.9) * mm});
            skLineSegment(sketch, "E71.MirrorCS", {"start": v(-78.1, 57.1) * mm, "end": v(-78.1, 65.7) * mm});
            skLineSegment(sketch, "E72.MirrorCS", {"start": v(-173.9, 89.9) * mm, "end": v(-163.9, 89.9) * mm});
            skLineSegment(sketch, "E73.MirrorCS", {"start": v(-116.7, 57.1) * mm, "end": v(-83.9, 89.9) * mm});
            skLineSegment(sketch, "E74.MirrorCS", {"start": v(-93.9, 89.9) * mm, "end": v(-83.9, 89.9) * mm});
            skLineSegment(sketch, "E75.MirrorCS", {"start": v(-186.7, 57.1) * mm, "end": v(-176.7, 57.1) * mm});
            skLineSegment(sketch, "E76.MirrorCS", {"start": v(-126.7, 57.1) * mm, "end": v(-116.7, 57.1) * mm});
            skLineSegment(sketch, "E77.MirrorCS", {"start": v(-166.7, 57.1) * mm, "end": v(-156.7, 57.1) * mm});
            skLineSegment(sketch, "E78.MirrorCS", {"start": v(-78.1, 75.7) * mm, "end": v(-78.1, 85.7) * mm});
            skLineSegment(sketch, "E79.MirrorCS", {"start": v(-206.7, 57.1) * mm, "end": v(-173.9, 89.9) * mm});
            skLineSegment(sketch, "E80.MirrorCS", {"start": v(-126.7, 57.1) * mm, "end": v(-93.9, 89.9) * mm});
            skLineSegment(sketch, "E81.MirrorCS", {"start": v(-206.7, 57.1) * mm, "end": v(-196.7, 57.1) * mm});
            skPoint(sketch, "E82.MirrorP", {"position": v(-203.9, 79.9) * mm});
            skLineSegment(sketch, "E83.MirrorCS", {"start": v(-166.7, 57.1) * mm, "end": v(-133.9, 89.9) * mm});
            skLineSegment(sketch, "E84.MirrorCS", {"start": v(-106.7, 57.1) * mm, "end": v(-96.7, 57.1) * mm});
            skPoint(sketch, "E85.MirrorP", {"position": v(-183.9, 79.9) * mm});
            skLineSegment(sketch, "E86.MirrorCS", {"start": v(-106.7, 57.1) * mm, "end": v(-78.1, 85.7) * mm});
            skPoint(sketch, "E87.MirrorP", {"position": v(-123.9, 79.9) * mm});
            skLineSegment(sketch, "E88.MirrorCS", {"start": v(-146.7, 57.1) * mm, "end": v(-113.9, 89.9) * mm});
            skLineSegment(sketch, "E89.MirrorCS", {"start": v(-96.7, 57.1) * mm, "end": v(-78.1, 75.7) * mm});
            skLineSegment(sketch, "E90.MirrorCS", {"start": v(-146.7, 57.1) * mm, "end": v(-136.7, 57.1) * mm});
            skLineSegment(sketch, "E91.MirrorCS", {"start": v(-133.9, 89.9) * mm, "end": v(-123.9, 89.9) * mm});
            skLineSegment(sketch, "E92.MirrorCS", {"start": v(-86.7, 57.1) * mm, "end": v(-78.1, 65.7) * mm});
            skLineSegment(sketch, "E93.MirrorCS", {"start": v(-193.9, 89.9) * mm, "end": v(-183.9, 89.9) * mm});
            skPoint(sketch, "E94.MirrorP", {"position": v(-63.9, 79.9) * mm});
            skPoint(sketch, "E95.MirrorP", {"position": v(-113.9, 79.9) * mm});
            skLineSegment(sketch, "E96.MirrorCS", {"start": v(-213.9, 69.9) * mm, "end": v(-193.9, 89.9) * mm});
            skPoint(sketch, "E97.MirrorP", {"position": v(-63.9, 89.9) * mm});
            skLineSegment(sketch, "E98.MirrorCS", {"start": v(-86.7, 57.1) * mm, "end": v(-78.1, 57.1) * mm});
            skLineSegment(sketch, "E99.MirrorCS", {"start": v(-113.9, 89.9) * mm, "end": v(-103.9, 89.9) * mm});
            skLineSegment(sketch, "E100.MirrorCS", {"start": v(-176.7, 57.1) * mm, "end": v(-143.9, 89.9) * mm});
            skPoint(sketch, "E101.MirrorP", {"position": v(-73.9, 79.9) * mm});
            skLineSegment(sketch, "E102.MirrorCS", {"start": v(-213.9, 79.9) * mm, "end": v(-203.9, 89.9) * mm});
            skPoint(sketch, "E103.MirrorP", {"position": v(-103.9, 79.9) * mm});
            skPoint(sketch, "E104.MirrorP", {"position": v(-73.9, 89.9) * mm});
            skLineSegment(sketch, "E105.MirrorCS", {"start": v(-153.9, 89.9) * mm, "end": v(-143.9, 89.9) * mm});
            skLineSegment(sketch, "E106.MirrorCS", {"start": v(-213.9, 79.9) * mm, "end": v(-213.9, 89.9) * mm});
            skPoint(sketch, "E107.MirrorP", {"position": v(-153.9, 79.9) * mm});
            skPoint(sketch, "E108.MirrorP", {"position": v(-163.9, 79.9) * mm});
            skLineSegment(sketch, "E109.MirrorCS", {"start": v(-213.9, 89.9) * mm, "end": v(-203.9, 89.9) * mm});
            skPoint(sketch, "E110.MirrorP", {"position": v(-193.9, 79.9) * mm});
            skPoint(sketch, "E111.MirrorP", {"position": v(-93.9, 79.9) * mm});
            skLineSegment(sketch, "E112.MirrorCS", {"start": v(-136.7, 57.1) * mm, "end": v(-103.9, 89.9) * mm});
            skLineSegment(sketch, "E113.MirrorCS", {"start": v(-156.7, 57.1) * mm, "end": v(-123.9, 89.9) * mm});
            skLineSegment(sketch, "E114.MirrorCS", {"start": v(-196.7, 57.1) * mm, "end": v(-163.9, 89.9) * mm});
            skPoint(sketch, "E115.MirrorP", {"position": v(-133.9, 79.9) * mm});
            skLineSegment(sketch, "E116", {"start": v(0, 0) * mm, "end": v(0, 120) * mm, "construction": true});
            skPoint(sketch, "E117.MirrorP", {"position": v(-53.9, 89.9) * mm});
            skLineSegment(sketch, "E118.MirrorCS", {"start": v(213.9, 89.9) * mm, "end": v(203.9, 89.9) * mm});
            skLineSegment(sketch, "E119.MirrorCS", {"start": v(78.1, 75.7) * mm, "end": v(78.1, 85.7) * mm});
            skLineSegment(sketch, "E120.MirrorCS", {"start": v(126.7, 57.1) * mm, "end": v(116.7, 57.1) * mm});
            skLineSegment(sketch, "E121.MirrorCS", {"start": v(93.9, 89.9) * mm, "end": v(83.9, 89.9) * mm});
            skLineSegment(sketch, "E122.MirrorCS", {"start": v(186.7, 57.1) * mm, "end": v(176.7, 57.1) * mm});
            skLineSegment(sketch, "E123.MirrorCS", {"start": v(206.7, 57.1) * mm, "end": v(196.7, 57.1) * mm});
            skLineSegment(sketch, "E124.MirrorCS", {"start": v(173.9, 89.9) * mm, "end": v(163.9, 89.9) * mm});
            skLineSegment(sketch, "E125.MirrorCS", {"start": v(213.9, 79.9) * mm, "end": v(213.9, 89.9) * mm});
            skLineSegment(sketch, "E126.MirrorCS", {"start": v(213.9, 59.9) * mm, "end": v(213.9, 69.9) * mm});
            skLineSegment(sketch, "E127.MirrorCS", {"start": v(193.9, 89.9) * mm, "end": v(183.9, 89.9) * mm});
            skLineSegment(sketch, "E128.MirrorCS", {"start": v(166.7, 57.1) * mm, "end": v(156.7, 57.1) * mm});
            skLineSegment(sketch, "E129.MirrorCS", {"start": v(86.7, 57.1) * mm, "end": v(78.1, 65.7) * mm});
            skLineSegment(sketch, "E130.MirrorCS", {"start": v(106.7, 57.1) * mm, "end": v(96.7, 57.1) * mm});
            skLineSegment(sketch, "E131.MirrorCS", {"start": v(133.9, 89.9) * mm, "end": v(123.9, 89.9) * mm});
            skLineSegment(sketch, "E132.MirrorCS", {"start": v(146.7, 57.1) * mm, "end": v(136.7, 57.1) * mm});
            skLineSegment(sketch, "E133.MirrorCS", {"start": v(78.1, 57.1) * mm, "end": v(78.1, 65.7) * mm});
            skLineSegment(sketch, "E134.MirrorCS", {"start": v(113.9, 89.9) * mm, "end": v(103.9, 89.9) * mm});
            skLineSegment(sketch, "E135.MirrorCS", {"start": v(86.7, 57.1) * mm, "end": v(78.1, 57.1) * mm});
            skLineSegment(sketch, "E136.MirrorCS", {"start": v(153.9, 89.9) * mm, "end": v(143.9, 89.9) * mm});
            skLineSegment(sketch, "E137.MirrorCS", {"start": v(213.9, 79.9) * mm, "end": v(203.9, 89.9) * mm});
            skLineSegment(sketch, "E138.MirrorCS", {"start": v(213.9, 69.9) * mm, "end": v(193.9, 89.9) * mm});
            skPoint(sketch, "E139.MirrorP", {"position": v(143.9, 79.9) * mm});
            skPoint(sketch, "E140.MirrorP", {"position": v(73.9, 89.9) * mm});
            skPoint(sketch, "E141.MirrorP", {"position": v(83.9, 79.9) * mm});
            skLineSegment(sketch, "E142.MirrorCS", {"start": v(96.7, 57.1) * mm, "end": v(78.1, 75.7) * mm});
            skLineSegment(sketch, "E143.MirrorCS", {"start": v(116.7, 57.1) * mm, "end": v(83.9, 89.9) * mm});
            skLineSegment(sketch, "E144.MirrorCS", {"start": v(196.7, 57.1) * mm, "end": v(163.9, 89.9) * mm});
            skPoint(sketch, "E145.MirrorP", {"position": v(153.9, 79.9) * mm});
            skLineSegment(sketch, "E146.MirrorCS", {"start": v(166.7, 57.1) * mm, "end": v(133.9, 89.9) * mm});
            skLineSegment(sketch, "E147.MirrorCS", {"start": v(156.7, 57.1) * mm, "end": v(123.9, 89.9) * mm});
            skLineSegment(sketch, "E148.MirrorCS", {"start": v(126.7, 57.1) * mm, "end": v(93.9, 89.9) * mm});
            skLineSegment(sketch, "E149.MirrorCS", {"start": v(106.7, 57.1) * mm, "end": v(78.1, 85.7) * mm});
            skPoint(sketch, "E150.MirrorP", {"position": v(203.9, 79.9) * mm});
            skLineSegment(sketch, "E151.MirrorCS", {"start": v(206.7, 57.1) * mm, "end": v(173.9, 89.9) * mm});
            skPoint(sketch, "E152.MirrorP", {"position": v(183.9, 79.9) * mm});
            skPoint(sketch, "E153.MirrorP", {"position": v(63.9, 79.9) * mm});
            skPoint(sketch, "E154.MirrorP", {"position": v(113.9, 79.9) * mm});
            skLineSegment(sketch, "E155.MirrorCS", {"start": v(213.9, 59.9) * mm, "end": v(183.9, 89.9) * mm});
            skPoint(sketch, "E156.MirrorP", {"position": v(173.9, 79.9) * mm});
            skLineSegment(sketch, "E157.MirrorCS", {"start": v(136.7, 57.1) * mm, "end": v(103.9, 89.9) * mm});
            skLineSegment(sketch, "E158.MirrorCS", {"start": v(176.7, 57.1) * mm, "end": v(143.9, 89.9) * mm});
            skPoint(sketch, "E159.MirrorP", {"position": v(123.9, 79.9) * mm});
            skPoint(sketch, "E160.MirrorP", {"position": v(103.9, 79.9) * mm});
            skPoint(sketch, "E161.MirrorP", {"position": v(63.9, 89.9) * mm});
            skPoint(sketch, "E162.MirrorP", {"position": v(93.9, 79.9) * mm});
            skLineSegment(sketch, "E163.MirrorCS", {"start": v(146.7, 57.1) * mm, "end": v(113.9, 89.9) * mm});
            skPoint(sketch, "E164.MirrorP", {"position": v(163.9, 79.9) * mm});
            skLineSegment(sketch, "E165.MirrorCS", {"start": v(186.7, 57.1) * mm, "end": v(153.9, 89.9) * mm});
            skPoint(sketch, "E166.MirrorP", {"position": v(73.9, 79.9) * mm});
            skPoint(sketch, "E167.MirrorP", {"position": v(193.9, 79.9) * mm});
            skPoint(sketch, "E168.MirrorP", {"position": v(133.9, 79.9) * mm});
            skPoint(sketch, "E169.MirrorP", {"position": v(53.9, 89.9) * mm});
            skLineSegment(sketch, "E170.MirrorCS", {"start": v(186.7, 42.9) * mm, "end": v(176.7, 42.9) * mm});
            skLineSegment(sketch, "E171.MirrorCS", {"start": v(173.9, 10.1) * mm, "end": v(163.9, 10.1) * mm});
            skLineSegment(sketch, "E172.MirrorCS", {"start": v(146.7, 42.9) * mm, "end": v(136.7, 42.9) * mm});
            skLineSegment(sketch, "E173.MirrorCS", {"start": v(206.7, 42.9) * mm, "end": v(196.7, 42.9) * mm});
            skLineSegment(sketch, "E174.MirrorCS", {"start": v(126.7, 42.9) * mm, "end": v(116.7, 42.9) * mm});
            skLineSegment(sketch, "E175.MirrorCS", {"start": v(78.1, 24.3) * mm, "end": v(78.1, 14.3) * mm});
            skLineSegment(sketch, "E176.MirrorCS", {"start": v(193.9, 10.1) * mm, "end": v(183.9, 10.1) * mm});
            skLineSegment(sketch, "E177.MirrorCS", {"start": v(213.9, 10.1) * mm, "end": v(203.9, 10.1) * mm});
            skLineSegment(sketch, "E178.MirrorCS", {"start": v(213.9, 20.1) * mm, "end": v(213.9, 10.1) * mm});
            skLineSegment(sketch, "E179.MirrorCS", {"start": v(153.9, 10.1) * mm, "end": v(143.9, 10.1) * mm});
            skLineSegment(sketch, "E180.MirrorCS", {"start": v(93.9, 10.1) * mm, "end": v(83.9, 10.1) * mm});
            skLineSegment(sketch, "E181.MirrorCS", {"start": v(106.7, 42.9) * mm, "end": v(96.7, 42.9) * mm});
            skLineSegment(sketch, "E182.MirrorCS", {"start": v(166.7, 42.9) * mm, "end": v(156.7, 42.9) * mm});
            skLineSegment(sketch, "E183.MirrorCS", {"start": v(78.1, 42.9) * mm, "end": v(78.1, 34.3) * mm});
            skLineSegment(sketch, "E184.MirrorCS", {"start": v(213.9, 40.1) * mm, "end": v(213.9, 30.1) * mm});
            skLineSegment(sketch, "E185.MirrorCS", {"start": v(86.7, 42.9) * mm, "end": v(78.1, 42.9) * mm});
            skLineSegment(sketch, "E186.MirrorCS", {"start": v(113.9, 10.1) * mm, "end": v(103.9, 10.1) * mm});
            skLineSegment(sketch, "E187.MirrorCS", {"start": v(133.9, 10.1) * mm, "end": v(123.9, 10.1) * mm});
            skLineSegment(sketch, "E188.MirrorCS", {"start": v(86.7, 42.9) * mm, "end": v(78.1, 34.3) * mm});
            skLineSegment(sketch, "E189.MirrorCS", {"start": v(213.9, 30.1) * mm, "end": v(193.9, 10.1) * mm});
            skLineSegment(sketch, "E190.MirrorCS", {"start": v(213.9, 20.1) * mm, "end": v(203.9, 10.1) * mm});
            skPoint(sketch, "E191.MirrorP", {"position": v(153.9, 20.1) * mm});
            skPoint(sketch, "E192.MirrorP", {"position": v(163.9, 20.1) * mm});
            skLineSegment(sketch, "E193.MirrorCS", {"start": v(146.7, 42.9) * mm, "end": v(113.9, 10.1) * mm});
            skPoint(sketch, "E194.MirrorP", {"position": v(93.9, 20.1) * mm});
            skPoint(sketch, "E195.MirrorP", {"position": v(63.9, 20.1) * mm});
            skPoint(sketch, "E196.MirrorP", {"position": v(123.9, 20.1) * mm});
            skPoint(sketch, "E197.MirrorP", {"position": v(133.9, 20.1) * mm});
            skPoint(sketch, "E198.MirrorP", {"position": v(63.9, 10.1) * mm});
            skPoint(sketch, "E199.MirrorP", {"position": v(143.9, 20.1) * mm});
            skLineSegment(sketch, "E200.MirrorCS", {"start": v(186.7, 42.9) * mm, "end": v(153.9, 10.1) * mm});
            skLineSegment(sketch, "E201.MirrorCS", {"start": v(196.7, 42.9) * mm, "end": v(163.9, 10.1) * mm});
            skPoint(sketch, "E202.MirrorP", {"position": v(203.9, 20.1) * mm});
            skPoint(sketch, "E203.MirrorP", {"position": v(173.9, 20.1) * mm});
            skPoint(sketch, "E204.MirrorP", {"position": v(193.9, 20.1) * mm});
            skLineSegment(sketch, "E205.MirrorCS", {"start": v(126.7, 42.9) * mm, "end": v(93.9, 10.1) * mm});
            skLineSegment(sketch, "E206.MirrorCS", {"start": v(136.7, 42.9) * mm, "end": v(103.9, 10.1) * mm});
            skPoint(sketch, "E207.MirrorP", {"position": v(113.9, 20.1) * mm});
            skPoint(sketch, "E208.MirrorP", {"position": v(183.9, 20.1) * mm});
            skLineSegment(sketch, "E209.MirrorCS", {"start": v(166.7, 42.9) * mm, "end": v(133.9, 10.1) * mm});
            skLineSegment(sketch, "E210.MirrorCS", {"start": v(106.7, 42.9) * mm, "end": v(78.1, 14.3) * mm});
            skLineSegment(sketch, "E211.MirrorCS", {"start": v(116.7, 42.9) * mm, "end": v(83.9, 10.1) * mm});
            skPoint(sketch, "E212.MirrorP", {"position": v(73.9, 10.1) * mm});
            skLineSegment(sketch, "E213.MirrorCS", {"start": v(156.7, 42.9) * mm, "end": v(123.9, 10.1) * mm});
            skLineSegment(sketch, "E214.MirrorCS", {"start": v(96.7, 42.9) * mm, "end": v(78.1, 24.3) * mm});
            skPoint(sketch, "E215.MirrorP", {"position": v(73.9, 20.1) * mm});
            skLineSegment(sketch, "E216.MirrorCS", {"start": v(176.7, 42.9) * mm, "end": v(143.9, 10.1) * mm});
            skPoint(sketch, "E217.MirrorP", {"position": v(103.9, 20.1) * mm});
            skLineSegment(sketch, "E218.MirrorCS", {"start": v(206.7, 42.9) * mm, "end": v(173.9, 10.1) * mm});
            skLineSegment(sketch, "E219.MirrorCS", {"start": v(213.9, 40.1) * mm, "end": v(183.9, 10.1) * mm});
            skPoint(sketch, "E220.MirrorP", {"position": v(83.9, 20.1) * mm});
            skPoint(sketch, "E221.MirrorP", {"position": v(53.9, 10.1) * mm});
            skSolve(sketch);
        }
        {
            var Q0;
            Q0 = qSketchRegion(id + "F22", true);
            extrude(context, id + "F23", {"entities" : qUnion([Q0]), "operationType" : NewBodyOperationType.REMOVE, "endBound" : BoundingType.THROUGH_ALL, "oppositeDirection" : true, "depth" : 25 * mm, "offsetDistance" : 25 * mm});
        }
        {
            var Q0;
            {var subQ0=makeQuery(id+"F9.opExtrude","CAP_FACE",FACE,{"disambiguationData":[OSD([sQuery(id+"F8.wireOp",EDGE,"E8.0.0"),sQuery(id+"F8.wireOp",EDGE,"E8.0.1"),sQuery(id+"F8.wireOp",EDGE,"E8.0.2"),sQuery(id+"F8.wireOp",EDGE,"E8.0.3"),sQuery(id+"F8.wireOp",EDGE,"E8.0.4"),sQuery(id+"F8.wireOp",EDGE,"E8.0.5"),sQuery(id+"F8.wireOp",EDGE,"E8.0.6"),sQuery(id+"F8.wireOp",EDGE,"E8.0.7"),sQuery(id+"F8.wireOp",EDGE,"E9.0.0"),sQuery(id+"F8.wireOp",EDGE,"E9.0.1"),sQuery(id+"F8.wireOp",EDGE,"E9.0.2"),sQuery(id+"F8.wireOp",EDGE,"E9.0.3"),sQuery(id+"F8.wireOp",EDGE,"E9.0.4"),sQuery(id+"F8.wireOp",EDGE,"E9.0.5"),sQuery(id+"F8.wireOp",EDGE,"E9.0.6"),sQuery(id+"F8.wireOp",EDGE,"E9.0.7")])],"isStart":true});var subQ2=sQuery(id+"F0.wireOp",EDGE,"E0.right");var subQ3=makeQuery(id+"F19.opPattern","COPY",FACE,{"derivedFrom":makeQuery(id+"F16.boolean.opBoolean","SPLIT",FACE,{"disambiguationData":[TD([subQ0])],"derivedFrom":makeQuery(id+"F16.opExtrude","SWEPT_FACE",FACE,{"disambiguationData":[OSD([sQuery(id+"F15.wireOp",EDGE,"E17.top")])]})}),"instanceName":"1"});var subQ4=sQuery(id+"F0.wireOp",EDGE,"E2.filletArc");var subQ5=makeQuery(id+"F1.opExtrude","SWEPT_FACE",FACE,{"disambiguationData":[OSD([subQ4])]});var subQ6=sQuery(id+"F0.wireOp",EDGE,"E3.filletArc");var subQ7=sQuery(id+"F0.wireOp",EDGE,"E0.left");var subQ8=makeQuery(id+"F1.opExtrude","CAP_FACE",FACE,{"disambiguationData":[OSD([sQuery(id+"F0.wireOp",EDGE,"E0.bottom"),sQuery(id+"F0.wireOp",EDGE,"E0.top"),subQ7,subQ2,sQuery(id+"F0.wireOp",EDGE,"E1.filletArc"),subQ4,subQ6,sQuery(id+"F0.wireOp",EDGE,"E4.filletArc")])],"isStart":true});Q0=makeQuery(id+"F21.boolean.opBoolean","SPLIT",FACE,{"disambiguationData":[TD([subQ3])],"derivedFrom":makeQuery(id+"F19.boolean.opBoolean","SPLIT",FACE,{"disambiguationData":[TD([subQ5])],"derivedFrom":makeQuery(id+"F9.boolean.opBoolean","SPLIT",FACE,{"disambiguationData":[TD([subQ8])],"derivedFrom":makeQuery(id+"F6.boolean.opBoolean","SPLIT",FACE,{"disambiguationData":[TD([subQ8])],"derivedFrom":makeQuery(id+"F1.opExtrude","SWEPT_FACE",FACE,{"disambiguationData":[OSD([subQ7])]})})})})});}
            var sketch = newSketch(context, id + "F24", { "sketchPlane" : qUnion([Q0])});
            skLineSegment(sketch, "E222.bottom", {"start": v(-112.5, 42) * mm, "end": v(-108.5, 42) * mm});
            skLineSegment(sketch, "E222.top", {"start": v(-112.5, 11) * mm, "end": v(-107.5, 11) * mm});
            skLineSegment(sketch, "E222.left", {"start": v(-112.5, 42) * mm, "end": v(-112.5, 41) * mm});
            skLineSegment(sketch, "E222.right", {"start": v(-71.5, 35) * mm, "end": v(-71.5, 30) * mm});
            skLineSegment(sketch, "E223", {"start": v(-112.5, 16) * mm, "end": v(-107.5, 11) * mm});
            skLineSegment(sketch, "E224.1.0.0", {"start": v(-112.5, 21) * mm, "end": v(-102.5, 11) * mm});
            skLineSegment(sketch, "E224.2.0.0", {"start": v(-112.5, 26) * mm, "end": v(-97.5, 11) * mm});
            skLineSegment(sketch, "E224.3.0.0", {"start": v(-112.5, 31) * mm, "end": v(-92.5, 11) * mm});
            skLineSegment(sketch, "E224.4.0.0", {"start": v(-112.5, 36) * mm, "end": v(-87.5, 11) * mm});
            skLineSegment(sketch, "E224.5.0.0", {"start": v(-112.5, 41) * mm, "end": v(-82.5, 11) * mm});
            skLineSegment(sketch, "E224.6.0.0", {"start": v(-108.5, 42) * mm, "end": v(-77.5, 11) * mm});
            skLineSegment(sketch, "E224.7.0.0", {"start": v(-103.5, 42) * mm, "end": v(-72.5, 11) * mm});
            skLineSegment(sketch, "E224.8.0.0", {"start": v(-98.5, 42) * mm, "end": v(-71.5, 15) * mm});
            skLineSegment(sketch, "E224.9.0.0", {"start": v(-93.5, 42) * mm, "end": v(-71.5, 20) * mm});
            skLineSegment(sketch, "E224.10.0.0", {"start": v(-88.5, 42) * mm, "end": v(-71.5, 25) * mm});
            skLineSegment(sketch, "E224.11.0.0", {"start": v(-83.5, 42) * mm, "end": v(-71.5, 30) * mm});
            skLineSegment(sketch, "E224.12.0.0", {"start": v(-78.5, 42) * mm, "end": v(-71.5, 35) * mm});
            skPoint(sketch, "E225.orphan", {"position": v(-107.5, 16) * mm});
            skPoint(sketch, "E226.orphan", {"position": v(-102.5, 16) * mm});
            skPoint(sketch, "E227.orphan", {"position": v(-97.5, 16) * mm});
            skPoint(sketch, "E228.orphan", {"position": v(-92.5, 16) * mm});
            skPoint(sketch, "E229.orphan", {"position": v(-87.5, 16) * mm});
            skPoint(sketch, "E230.orphan", {"position": v(-82.5, 16) * mm});
            skPoint(sketch, "E231.orphan", {"position": v(-77.5, 16) * mm});
            skPoint(sketch, "E232.orphan", {"position": v(-72.5, 16) * mm});
            skPoint(sketch, "E233.orphan", {"position": v(-67.5, 16) * mm});
            skPoint(sketch, "E234.orphan", {"position": v(-62.5, 16) * mm});
            skPoint(sketch, "E235.orphan", {"position": v(-57.5, 16) * mm});
            skPoint(sketch, "E236.orphan", {"position": v(-52.5, 16) * mm});
            skPoint(sketch, "E237.orphan", {"position": v(-47.5, 11) * mm});
            skPoint(sketch, "E238.orphan", {"position": v(-52.5, 11) * mm});
            skPoint(sketch, "E239.orphan", {"position": v(-57.5, 11) * mm});
            skPoint(sketch, "E240.orphan", {"position": v(-62.5, 11) * mm});
            skPoint(sketch, "E241.orphan", {"position": v(-67.5, 11) * mm});
            skLineSegment(sketch, "E242.trimOffspring", {"start": v(-112.5, 16) * mm, "end": v(-112.5, 11) * mm});
            skLineSegment(sketch, "E243.trimOffspring", {"start": v(-92.5, 11) * mm, "end": v(-87.5, 11) * mm});
            skLineSegment(sketch, "E244.trimOffspring", {"start": v(-112.5, 26) * mm, "end": v(-112.5, 21) * mm});
            skLineSegment(sketch, "E245.trimOffspring", {"start": v(-102.5, 11) * mm, "end": v(-97.5, 11) * mm});
            skLineSegment(sketch, "E246.trimOffspring", {"start": v(-82.5, 11) * mm, "end": v(-77.5, 11) * mm});
            skLineSegment(sketch, "E247.trimOffspring", {"start": v(-112.5, 36) * mm, "end": v(-112.5, 31) * mm});
            skLineSegment(sketch, "E248.trimOffspring", {"start": v(-72.5, 11) * mm, "end": v(-71.5, 11) * mm});
            skLineSegment(sketch, "E249.trimOffspring", {"start": v(-103.5, 42) * mm, "end": v(-98.5, 42) * mm});
            skLineSegment(sketch, "E250.trimOffspring", {"start": v(-71.5, 15) * mm, "end": v(-71.5, 11) * mm});
            skLineSegment(sketch, "E251.trimOffspring", {"start": v(-93.5, 42) * mm, "end": v(-88.5, 42) * mm});
            skLineSegment(sketch, "E252.trimOffspring", {"start": v(-83.5, 42) * mm, "end": v(-78.5, 42) * mm});
            skLineSegment(sketch, "E253.trimOffspring", {"start": v(-71.5, 25) * mm, "end": v(-71.5, 20) * mm});
            skLineSegment(sketch, "E254", {"start": v(-66, 50) * mm, "end": v(66, 50) * mm, "construction": true});
            skLineSegment(sketch, "E255.MirrorCS", {"start": v(-112.5, 58) * mm, "end": v(-112.5, 59) * mm});
            skLineSegment(sketch, "E256.MirrorCS", {"start": v(-72.5, 89) * mm, "end": v(-71.5, 89) * mm});
            skLineSegment(sketch, "E257.MirrorCS", {"start": v(-71.5, 85) * mm, "end": v(-71.5, 89) * mm});
            skLineSegment(sketch, "E258.MirrorCS", {"start": v(-102.5, 89) * mm, "end": v(-97.5, 89) * mm});
            skLineSegment(sketch, "E259.MirrorCS", {"start": v(-112.5, 89) * mm, "end": v(-107.5, 89) * mm});
            skLineSegment(sketch, "E260.MirrorCS", {"start": v(-112.5, 64) * mm, "end": v(-112.5, 69) * mm});
            skLineSegment(sketch, "E261.MirrorCS", {"start": v(-112.5, 84) * mm, "end": v(-107.5, 89) * mm});
            skLineSegment(sketch, "E262.MirrorCS", {"start": v(-112.5, 74) * mm, "end": v(-112.5, 79) * mm});
            skLineSegment(sketch, "E263.MirrorCS", {"start": v(-83.5, 58) * mm, "end": v(-78.5, 58) * mm});
            skLineSegment(sketch, "E264.MirrorCS", {"start": v(-71.5, 65) * mm, "end": v(-71.5, 70) * mm});
            skLineSegment(sketch, "E265.MirrorCS", {"start": v(-112.5, 58) * mm, "end": v(-108.5, 58) * mm});
            skLineSegment(sketch, "E266.MirrorCS", {"start": v(-71.5, 75) * mm, "end": v(-71.5, 80) * mm});
            skLineSegment(sketch, "E267.MirrorCS", {"start": v(-93.5, 58) * mm, "end": v(-88.5, 58) * mm});
            skLineSegment(sketch, "E268.MirrorCS", {"start": v(-112.5, 84) * mm, "end": v(-112.5, 89) * mm});
            skLineSegment(sketch, "E269.MirrorCS", {"start": v(-92.5, 89) * mm, "end": v(-87.5, 89) * mm});
            skLineSegment(sketch, "E270.MirrorCS", {"start": v(-82.5, 89) * mm, "end": v(-77.5, 89) * mm});
            skLineSegment(sketch, "E271.MirrorCS", {"start": v(-103.5, 58) * mm, "end": v(-98.5, 58) * mm});
            skPoint(sketch, "E272.MirrorP", {"position": v(-57.5, 89) * mm});
            skLineSegment(sketch, "E273.MirrorCS", {"start": v(-112.5, 79) * mm, "end": v(-102.5, 89) * mm});
            skPoint(sketch, "E274.MirrorP", {"position": v(-87.5, 84) * mm});
            skPoint(sketch, "E275.MirrorP", {"position": v(-62.5, 84) * mm});
            skLineSegment(sketch, "E276.MirrorCS", {"start": v(-103.5, 58) * mm, "end": v(-72.5, 89) * mm});
            skPoint(sketch, "E277.MirrorP", {"position": v(-57.5, 84) * mm});
            skLineSegment(sketch, "E278.MirrorCS", {"start": v(-112.5, 74) * mm, "end": v(-97.5, 89) * mm});
            skPoint(sketch, "E279.MirrorP", {"position": v(-97.5, 84) * mm});
            skPoint(sketch, "E280.MirrorP", {"position": v(-62.5, 89) * mm});
            skLineSegment(sketch, "E281.MirrorCS", {"start": v(-88.5, 58) * mm, "end": v(-71.5, 75) * mm});
            skPoint(sketch, "E282.MirrorP", {"position": v(-67.5, 84) * mm});
            skLineSegment(sketch, "E283.MirrorCS", {"start": v(-108.5, 58) * mm, "end": v(-77.5, 89) * mm});
            skPoint(sketch, "E284.MirrorP", {"position": v(-82.5, 84) * mm});
            skPoint(sketch, "E285.MirrorP", {"position": v(-72.5, 84) * mm});
            skPoint(sketch, "E286.MirrorP", {"position": v(-67.5, 89) * mm});
            skPoint(sketch, "E287.MirrorP", {"position": v(-107.5, 84) * mm});
            skLineSegment(sketch, "E288.MirrorCS", {"start": v(-98.5, 58) * mm, "end": v(-71.5, 85) * mm});
            skPoint(sketch, "E289.MirrorP", {"position": v(-52.5, 84) * mm});
            skLineSegment(sketch, "E290.MirrorCS", {"start": v(-112.5, 69) * mm, "end": v(-92.5, 89) * mm});
            skLineSegment(sketch, "E291.MirrorCS", {"start": v(-112.5, 59) * mm, "end": v(-82.5, 89) * mm});
            skPoint(sketch, "E292.MirrorP", {"position": v(-47.5, 89) * mm});
            skLineSegment(sketch, "E293.MirrorCS", {"start": v(-112.5, 64) * mm, "end": v(-87.5, 89) * mm});
            skPoint(sketch, "E294.MirrorP", {"position": v(-92.5, 84) * mm});
            skLineSegment(sketch, "E295.MirrorCS", {"start": v(-78.5, 58) * mm, "end": v(-71.5, 65) * mm});
            skPoint(sketch, "E296.MirrorP", {"position": v(-52.5, 89) * mm});
            skLineSegment(sketch, "E297.MirrorCS", {"start": v(-93.5, 58) * mm, "end": v(-71.5, 80) * mm});
            skPoint(sketch, "E298.MirrorP", {"position": v(-102.5, 84) * mm});
            skPoint(sketch, "E299.MirrorP", {"position": v(-77.5, 84) * mm});
            skLineSegment(sketch, "E300.MirrorCS", {"start": v(-83.5, 58) * mm, "end": v(-71.5, 70) * mm});
            skLineSegment(sketch, "E301", {"start": v(0, 0) * mm, "end": v(0, 120) * mm, "construction": true});
            skLineSegment(sketch, "E302.MirrorCS", {"start": v(112.5, 58) * mm, "end": v(108.5, 58) * mm});
            skLineSegment(sketch, "E303.MirrorCS", {"start": v(72.5, 11) * mm, "end": v(71.5, 11) * mm});
            skLineSegment(sketch, "E304.MirrorCS", {"start": v(112.5, 58) * mm, "end": v(112.5, 59) * mm});
            skLineSegment(sketch, "E305.MirrorCS", {"start": v(72.5, 89) * mm, "end": v(71.5, 89) * mm});
            skLineSegment(sketch, "E306.MirrorCS", {"start": v(71.5, 15) * mm, "end": v(71.5, 11) * mm});
            skLineSegment(sketch, "E307.MirrorCS", {"start": v(112.5, 42) * mm, "end": v(112.5, 41) * mm});
            skLineSegment(sketch, "E308.MirrorCS", {"start": v(112.5, 42) * mm, "end": v(108.5, 42) * mm});
            skLineSegment(sketch, "E309.MirrorCS", {"start": v(112.5, 26) * mm, "end": v(112.5, 21) * mm});
            skLineSegment(sketch, "E310.MirrorCS", {"start": v(93.5, 58) * mm, "end": v(88.5, 58) * mm});
            skLineSegment(sketch, "E311.MirrorCS", {"start": v(93.5, 42) * mm, "end": v(88.5, 42) * mm});
            skLineSegment(sketch, "E312.MirrorCS", {"start": v(92.5, 11) * mm, "end": v(87.5, 11) * mm});
            skLineSegment(sketch, "E313.MirrorCS", {"start": v(71.5, 75) * mm, "end": v(71.5, 80) * mm});
            skLineSegment(sketch, "E314.MirrorCS", {"start": v(112.5, 16) * mm, "end": v(107.5, 11) * mm});
            skLineSegment(sketch, "E315.MirrorCS", {"start": v(71.5, 25) * mm, "end": v(71.5, 20) * mm});
            skLineSegment(sketch, "E316.MirrorCS", {"start": v(71.5, 35) * mm, "end": v(71.5, 30) * mm});
            skLineSegment(sketch, "E317.MirrorCS", {"start": v(112.5, 84) * mm, "end": v(112.5, 89) * mm});
            skLineSegment(sketch, "E318.MirrorCS", {"start": v(112.5, 84) * mm, "end": v(107.5, 89) * mm});
            skLineSegment(sketch, "E319.MirrorCS", {"start": v(82.5, 89) * mm, "end": v(77.5, 89) * mm});
            skLineSegment(sketch, "E320.MirrorCS", {"start": v(102.5, 11) * mm, "end": v(97.5, 11) * mm});
            skLineSegment(sketch, "E321.MirrorCS", {"start": v(112.5, 11) * mm, "end": v(107.5, 11) * mm});
            skLineSegment(sketch, "E322.MirrorCS", {"start": v(71.5, 65) * mm, "end": v(71.5, 70) * mm});
            skLineSegment(sketch, "E323.MirrorCS", {"start": v(71.5, 85) * mm, "end": v(71.5, 89) * mm});
            skLineSegment(sketch, "E324.MirrorCS", {"start": v(82.5, 11) * mm, "end": v(77.5, 11) * mm});
            skLineSegment(sketch, "E325.MirrorCS", {"start": v(103.5, 58) * mm, "end": v(98.5, 58) * mm});
            skLineSegment(sketch, "E326.MirrorCS", {"start": v(112.5, 89) * mm, "end": v(107.5, 89) * mm});
            skLineSegment(sketch, "E327.MirrorCS", {"start": v(112.5, 74) * mm, "end": v(112.5, 79) * mm});
            skLineSegment(sketch, "E328.MirrorCS", {"start": v(112.5, 36) * mm, "end": v(112.5, 31) * mm});
            skLineSegment(sketch, "E329.MirrorCS", {"start": v(112.5, 64) * mm, "end": v(112.5, 69) * mm});
            skLineSegment(sketch, "E330.MirrorCS", {"start": v(83.5, 58) * mm, "end": v(78.5, 58) * mm});
            skLineSegment(sketch, "E331.MirrorCS", {"start": v(92.5, 89) * mm, "end": v(87.5, 89) * mm});
            skLineSegment(sketch, "E332.MirrorCS", {"start": v(112.5, 21) * mm, "end": v(102.5, 11) * mm});
            skLineSegment(sketch, "E333.MirrorCS", {"start": v(102.5, 89) * mm, "end": v(97.5, 89) * mm});
            skLineSegment(sketch, "E334.MirrorCS", {"start": v(103.5, 42) * mm, "end": v(98.5, 42) * mm});
            skLineSegment(sketch, "E335.MirrorCS", {"start": v(112.5, 26) * mm, "end": v(97.5, 11) * mm});
            skLineSegment(sketch, "E336.MirrorCS", {"start": v(112.5, 16) * mm, "end": v(112.5, 11) * mm});
            skLineSegment(sketch, "E337.MirrorCS", {"start": v(78.5, 42) * mm, "end": v(71.5, 35) * mm});
            skLineSegment(sketch, "E338.MirrorCS", {"start": v(83.5, 42) * mm, "end": v(78.5, 42) * mm});
            skLineSegment(sketch, "E339.MirrorCS", {"start": v(78.5, 58) * mm, "end": v(71.5, 65) * mm});
            skPoint(sketch, "E340.MirrorP", {"position": v(57.5, 11) * mm});
            skPoint(sketch, "E341.MirrorP", {"position": v(57.5, 16) * mm});
            skPoint(sketch, "E342.MirrorP", {"position": v(57.5, 89) * mm});
            skPoint(sketch, "E343.MirrorP", {"position": v(82.5, 84) * mm});
            skPoint(sketch, "E344.MirrorP", {"position": v(72.5, 16) * mm});
            skPoint(sketch, "E345.MirrorP", {"position": v(67.5, 84) * mm});
            skPoint(sketch, "E346.MirrorP", {"position": v(102.5, 16) * mm});
            skLineSegment(sketch, "E347.MirrorCS", {"start": v(112.5, 74) * mm, "end": v(97.5, 89) * mm});
            skPoint(sketch, "E348.MirrorP", {"position": v(92.5, 16) * mm});
            skLineSegment(sketch, "E349.MirrorCS", {"start": v(112.5, 79) * mm, "end": v(102.5, 89) * mm});
            skPoint(sketch, "E350.MirrorP", {"position": v(92.5, 84) * mm});
            skPoint(sketch, "E351.MirrorP", {"position": v(102.5, 84) * mm});
            skPoint(sketch, "E352.MirrorP", {"position": v(67.5, 89) * mm});
            skPoint(sketch, "E353.MirrorP", {"position": v(62.5, 11) * mm});
            skLineSegment(sketch, "E354.MirrorCS", {"start": v(88.5, 58) * mm, "end": v(71.5, 75) * mm});
            skPoint(sketch, "E355.MirrorP", {"position": v(107.5, 16) * mm});
            skPoint(sketch, "E356.MirrorP", {"position": v(62.5, 84) * mm});
            skLineSegment(sketch, "E357.MirrorCS", {"start": v(112.5, 36) * mm, "end": v(87.5, 11) * mm});
            skLineSegment(sketch, "E358.MirrorCS", {"start": v(93.5, 42) * mm, "end": v(71.5, 20) * mm});
            skLineSegment(sketch, "E359.MirrorCS", {"start": v(93.5, 58) * mm, "end": v(71.5, 80) * mm});
            skPoint(sketch, "E360.MirrorP", {"position": v(107.5, 84) * mm});
            skLineSegment(sketch, "E361.MirrorCS", {"start": v(112.5, 31) * mm, "end": v(92.5, 11) * mm});
            skLineSegment(sketch, "E362.MirrorCS", {"start": v(108.5, 42) * mm, "end": v(77.5, 11) * mm});
            skLineSegment(sketch, "E363.MirrorCS", {"start": v(108.5, 58) * mm, "end": v(77.5, 89) * mm});
            skLineSegment(sketch, "E364.MirrorCS", {"start": v(112.5, 59) * mm, "end": v(82.5, 89) * mm});
            skPoint(sketch, "E365.MirrorP", {"position": v(52.5, 84) * mm});
            skPoint(sketch, "E366.MirrorP", {"position": v(87.5, 84) * mm});
            skLineSegment(sketch, "E367.MirrorCS", {"start": v(98.5, 58) * mm, "end": v(71.5, 85) * mm});
            skPoint(sketch, "E368.MirrorP", {"position": v(97.5, 84) * mm});
            skPoint(sketch, "E369.MirrorP", {"position": v(87.5, 16) * mm});
            skPoint(sketch, "E370.MirrorP", {"position": v(57.5, 84) * mm});
            skPoint(sketch, "E371.MirrorP", {"position": v(82.5, 16) * mm});
            skLineSegment(sketch, "E372.MirrorCS", {"start": v(112.5, 64) * mm, "end": v(87.5, 89) * mm});
            skLineSegment(sketch, "E373.MirrorCS", {"start": v(103.5, 42) * mm, "end": v(72.5, 11) * mm});
            skPoint(sketch, "E374.MirrorP", {"position": v(67.5, 11) * mm});
            skPoint(sketch, "E375.MirrorP", {"position": v(67.5, 16) * mm});
            skLineSegment(sketch, "E376.MirrorCS", {"start": v(103.5, 58) * mm, "end": v(72.5, 89) * mm});
            skLineSegment(sketch, "E377.MirrorCS", {"start": v(83.5, 58) * mm, "end": v(71.5, 70) * mm});
            skPoint(sketch, "E378.MirrorP", {"position": v(72.5, 84) * mm});
            skPoint(sketch, "E379.MirrorP", {"position": v(97.5, 16) * mm});
            skPoint(sketch, "E380.MirrorP", {"position": v(52.5, 89) * mm});
            skLineSegment(sketch, "E381.MirrorCS", {"start": v(112.5, 69) * mm, "end": v(92.5, 89) * mm});
            skPoint(sketch, "E382.MirrorP", {"position": v(77.5, 84) * mm});
            skLineSegment(sketch, "E383.MirrorCS", {"start": v(112.5, 41) * mm, "end": v(82.5, 11) * mm});
            skPoint(sketch, "E384.MirrorP", {"position": v(47.5, 89) * mm});
            skLineSegment(sketch, "E385.MirrorCS", {"start": v(88.5, 42) * mm, "end": v(71.5, 25) * mm});
            skPoint(sketch, "E386.MirrorP", {"position": v(77.5, 16) * mm});
            skPoint(sketch, "E387.MirrorP", {"position": v(62.5, 89) * mm});
            skLineSegment(sketch, "E388.MirrorCS", {"start": v(98.5, 42) * mm, "end": v(71.5, 15) * mm});
            skLineSegment(sketch, "E389.MirrorCS", {"start": v(83.5, 42) * mm, "end": v(71.5, 30) * mm});
            skPoint(sketch, "E390.MirrorP", {"position": v(52.5, 16) * mm});
            skPoint(sketch, "E391.MirrorP", {"position": v(62.5, 16) * mm});
            skPoint(sketch, "E392.MirrorP", {"position": v(47.5, 11) * mm});
            skPoint(sketch, "E393.MirrorP", {"position": v(52.5, 11) * mm});
            skSolve(sketch);
        }
        {
            var Q0;
            Q0 = qSketchRegion(id + "F24", true);
            extrude(context, id + "F25", {"entities" : qUnion([Q0]), "operationType" : NewBodyOperationType.REMOVE, "endBound" : BoundingType.THROUGH_ALL, "oppositeDirection" : true, "depth" : 25 * mm, "offsetDistance" : 25 * mm});
        }
        {
            var Q0;
            {var subQ0=makeQuery(id+"F6.opExtrude","CAP_FACE",FACE,{"disambiguationData":[OSD([sQuery(id+"F5.wireOp",EDGE,"E6.0.0"),sQuery(id+"F5.wireOp",EDGE,"E6.0.1"),sQuery(id+"F5.wireOp",EDGE,"E6.0.2"),sQuery(id+"F5.wireOp",EDGE,"E6.0.3"),sQuery(id+"F5.wireOp",EDGE,"E6.0.4"),sQuery(id+"F5.wireOp",EDGE,"E6.0.5"),sQuery(id+"F5.wireOp",EDGE,"E6.0.6"),sQuery(id+"F5.wireOp",EDGE,"E6.0.7"),sQuery(id+"F5.wireOp",EDGE,"E7.0.0"),sQuery(id+"F5.wireOp",EDGE,"E7.0.1"),sQuery(id+"F5.wireOp",EDGE,"E7.0.2"),sQuery(id+"F5.wireOp",EDGE,"E7.0.3"),sQuery(id+"F5.wireOp",EDGE,"E7.0.4"),sQuery(id+"F5.wireOp",EDGE,"E7.0.5"),sQuery(id+"F5.wireOp",EDGE,"E7.0.6"),sQuery(id+"F5.wireOp",EDGE,"E7.0.7")])],"isStart":true});var subQ2=sQuery(id+"F0.wireOp",EDGE,"E0.right");var subQ3=makeQuery(id+"F19.opPattern","COPY",FACE,{"derivedFrom":makeQuery(id+"F16.boolean.opBoolean","SPLIT",FACE,{"disambiguationData":[TD([subQ0])],"derivedFrom":makeQuery(id+"F16.opExtrude","SWEPT_FACE",FACE,{"disambiguationData":[OSD([sQuery(id+"F15.wireOp",EDGE,"E17.top")])]})}),"instanceName":"1"});var subQ4=sQuery(id+"F0.wireOp",EDGE,"E2.filletArc");var subQ5=makeQuery(id+"F1.opExtrude","SWEPT_FACE",FACE,{"disambiguationData":[OSD([subQ4])]});var subQ6=sQuery(id+"F0.wireOp",EDGE,"E3.filletArc");var subQ8=sQuery(id+"F0.wireOp",EDGE,"E0.left");Q0=makeQuery(id+"F21.boolean.opBoolean","SPLIT",FACE,{"disambiguationData":[TD([subQ3])],"derivedFrom":makeQuery(id+"F19.boolean.opBoolean","SPLIT",FACE,{"disambiguationData":[TD([subQ5])],"derivedFrom":makeQuery(id+"F9.boolean.opBoolean","SPLIT",FACE,{"disambiguationData":[TD([subQ0])],"derivedFrom":makeQuery(id+"F6.boolean.opBoolean","SPLIT",FACE,{"disambiguationData":[TD([makeQuery(id+"F1.opExtrude","CAP_FACE",FACE,{"disambiguationData":[OSD([sQuery(id+"F0.wireOp",EDGE,"E0.bottom"),sQuery(id+"F0.wireOp",EDGE,"E0.top"),subQ8,subQ2,sQuery(id+"F0.wireOp",EDGE,"E1.filletArc"),subQ4,subQ6,sQuery(id+"F0.wireOp",EDGE,"E4.filletArc")])],"isStart":true})])],"derivedFrom":makeQuery(id+"F1.opExtrude","SWEPT_FACE",FACE,{"disambiguationData":[OSD([subQ8])]})})})})});}
            var sketch = newSketch(context, id + "F26", { "sketchPlane" : qUnion([Q0])});
            skLineSegment(sketch, "E394.bottom", {"start": v(-49, 95) * mm, "end": v(49, 95) * mm});
            skLineSegment(sketch, "E394.top", {"start": v(-49, 61) * mm, "end": v(49, 61) * mm});
            skArc(sketch, "E395", {"start": v(-49, 95) * mm, "mid": v(-66, 78) * mm, "end": v(-49, 61) * mm});
            skArc(sketch, "E396", {"start": v(49, 61) * mm, "mid": v(66, 78) * mm, "end": v(49, 95) * mm});
            skSolve(sketch);
        }
        {
            var Q0;
            Q0 = qSketchRegion(id + "F26", true);
            extrude(context, id + "F27", {"entities" : qUnion([Q0]), "operationType" : NewBodyOperationType.REMOVE, "endBound" : BoundingType.THROUGH_ALL, "oppositeDirection" : true, "depth" : 25 * mm, "offsetDistance" : 25 * mm});
        }
        {
            var Q0;
            {var subQ0=sQuery(id+"F0.wireOp",EDGE,"E0.right");var subQ1=makeQuery(id+"F9.opExtrude","CAP_FACE",FACE,{"disambiguationData":[OSD([sQuery(id+"F8.wireOp",EDGE,"E8.0.0"),sQuery(id+"F8.wireOp",EDGE,"E8.0.1"),sQuery(id+"F8.wireOp",EDGE,"E8.0.2"),sQuery(id+"F8.wireOp",EDGE,"E8.0.3"),sQuery(id+"F8.wireOp",EDGE,"E8.0.4"),sQuery(id+"F8.wireOp",EDGE,"E8.0.5"),sQuery(id+"F8.wireOp",EDGE,"E8.0.6"),sQuery(id+"F8.wireOp",EDGE,"E8.0.7"),sQuery(id+"F8.wireOp",EDGE,"E9.0.0"),sQuery(id+"F8.wireOp",EDGE,"E9.0.1"),sQuery(id+"F8.wireOp",EDGE,"E9.0.2"),sQuery(id+"F8.wireOp",EDGE,"E9.0.3"),sQuery(id+"F8.wireOp",EDGE,"E9.0.4"),sQuery(id+"F8.wireOp",EDGE,"E9.0.5"),sQuery(id+"F8.wireOp",EDGE,"E9.0.6"),sQuery(id+"F8.wireOp",EDGE,"E9.0.7")])],"isStart":false});var subQ2=makeQuery(id+"F6.opExtrude","CAP_FACE",FACE,{"disambiguationData":[OSD([sQuery(id+"F5.wireOp",EDGE,"E6.0.0"),sQuery(id+"F5.wireOp",EDGE,"E6.0.1"),sQuery(id+"F5.wireOp",EDGE,"E6.0.2"),sQuery(id+"F5.wireOp",EDGE,"E6.0.3"),sQuery(id+"F5.wireOp",EDGE,"E6.0.4"),sQuery(id+"F5.wireOp",EDGE,"E6.0.5"),sQuery(id+"F5.wireOp",EDGE,"E6.0.6"),sQuery(id+"F5.wireOp",EDGE,"E6.0.7"),sQuery(id+"F5.wireOp",EDGE,"E7.0.0"),sQuery(id+"F5.wireOp",EDGE,"E7.0.1"),sQuery(id+"F5.wireOp",EDGE,"E7.0.2"),sQuery(id+"F5.wireOp",EDGE,"E7.0.3"),sQuery(id+"F5.wireOp",EDGE,"E7.0.4"),sQuery(id+"F5.wireOp",EDGE,"E7.0.5"),sQuery(id+"F5.wireOp",EDGE,"E7.0.6"),sQuery(id+"F5.wireOp",EDGE,"E7.0.7")])],"isStart":true});var subQ3=makeQuery(id+"F19.opPattern","COPY",FACE,{"derivedFrom":makeQuery(id+"F16.boolean.opBoolean","SPLIT",FACE,{"disambiguationData":[TD([subQ2])],"derivedFrom":makeQuery(id+"F16.opExtrude","SWEPT_FACE",FACE,{"disambiguationData":[OSD([sQuery(id+"F15.wireOp",EDGE,"E17.top")])]})}),"instanceName":"1"});var subQ4=makeQuery(id+"F21.opPattern","COPY",FACE,{"derivedFrom":subQ3,"instanceName":"1"});var subQ5=sQuery(id+"F0.wireOp",EDGE,"E0.left");var subQ6=makeQuery(id+"F1.opExtrude","SWEPT_FACE",FACE,{"disambiguationData":[OSD([subQ5])]});var subQ7=sQuery(id+"F0.wireOp",EDGE,"E2.filletArc");var subQ8=makeQuery(id+"F1.opExtrude","SWEPT_FACE",FACE,{"disambiguationData":[OSD([subQ7])]});var subQ9=sQuery(id+"F0.wireOp",EDGE,"E3.filletArc");Q0=makeQuery(id+"F27.boolean.opBoolean","SPLIT",FACE,{"disambiguationData":[TD([subQ6,subQ1,subQ3,subQ4,makeQuery(id+"F27.opExtrude","SWEPT_FACE",FACE,{"disambiguationData":[OSD([sQuery(id+"F26.wireOp",EDGE,"E394.top")])]}),makeQuery(id+"F27.opExtrude","SWEPT_FACE",FACE,{"disambiguationData":[OSD([sQuery(id+"F26.wireOp",EDGE,"E395")])]}),makeQuery(id+"F27.opExtrude","SWEPT_FACE",FACE,{"disambiguationData":[OSD([sQuery(id+"F26.wireOp",EDGE,"E396")])]})])],"derivedFrom":makeQuery(id+"F21.boolean.opBoolean","SPLIT",FACE,{"disambiguationData":[TD([subQ3])],"derivedFrom":makeQuery(id+"F19.boolean.opBoolean","SPLIT",FACE,{"disambiguationData":[TD([subQ8])],"derivedFrom":makeQuery(id+"F9.boolean.opBoolean","SPLIT",FACE,{"disambiguationData":[TD([subQ2])],"derivedFrom":makeQuery(id+"F6.boolean.opBoolean","SPLIT",FACE,{"disambiguationData":[TD([makeQuery(id+"F1.opExtrude","CAP_FACE",FACE,{"disambiguationData":[OSD([sQuery(id+"F0.wireOp",EDGE,"E0.bottom"),sQuery(id+"F0.wireOp",EDGE,"E0.top"),subQ5,subQ0,sQuery(id+"F0.wireOp",EDGE,"E1.filletArc"),subQ7,subQ9,sQuery(id+"F0.wireOp",EDGE,"E4.filletArc")])],"isStart":true})])],"derivedFrom":subQ6})})})})});}
            var sketch = newSketch(context, id + "F28", { "sketchPlane" : qUnion([Q0])});
            skLineSegment(sketch, "E397.bottom", {"start": v(-66, 61) * mm, "end": v(66, 61) * mm});
            skLineSegment(sketch, "E397.top", {"start": v(-66, 59) * mm, "end": v(66, 59) * mm});
            skLineSegment(sketch, "E397.left", {"start": v(-66, 61) * mm, "end": v(-66, 59) * mm});
            skLineSegment(sketch, "E397.right", {"start": v(66, 61) * mm, "end": v(66, 59) * mm});
            skSolve(sketch);
        }
        {
            var Q0;
            Q0 = qSketchRegion(id + "F28", true);
            var Q1;
            Q1=makeQuery(id+"F19.opPattern","COPY",FACE,{"derivedFrom":makeQuery(id+"F16.boolean.opBoolean","SPLIT",FACE,{"disambiguationData":[TD([makeQuery(id+"F6.opExtrude","CAP_FACE",FACE,{"disambiguationData":[OSD([sQuery(id+"F5.wireOp",EDGE,"E6.0.0"),sQuery(id+"F5.wireOp",EDGE,"E6.0.1"),sQuery(id+"F5.wireOp",EDGE,"E6.0.2"),sQuery(id+"F5.wireOp",EDGE,"E6.0.3"),sQuery(id+"F5.wireOp",EDGE,"E6.0.4"),sQuery(id+"F5.wireOp",EDGE,"E6.0.5"),sQuery(id+"F5.wireOp",EDGE,"E6.0.6"),sQuery(id+"F5.wireOp",EDGE,"E6.0.7"),sQuery(id+"F5.wireOp",EDGE,"E7.0.0"),sQuery(id+"F5.wireOp",EDGE,"E7.0.1"),sQuery(id+"F5.wireOp",EDGE,"E7.0.2"),sQuery(id+"F5.wireOp",EDGE,"E7.0.3"),sQuery(id+"F5.wireOp",EDGE,"E7.0.4"),sQuery(id+"F5.wireOp",EDGE,"E7.0.5"),sQuery(id+"F5.wireOp",EDGE,"E7.0.6"),sQuery(id+"F5.wireOp",EDGE,"E7.0.7")])],"isStart":true})])],"derivedFrom":makeQuery(id+"F16.opExtrude","SWEPT_FACE",FACE,{"disambiguationData":[OSD([sQuery(id+"F15.wireOp",EDGE,"E17.right")])]})}),"instanceName":"1"});
            extrude(context, id + "F29", {"entities" : qUnion([Q0]), "operationType" : NewBodyOperationType.ADD, "endBound" : BoundingType.UP_TO_SURFACE, "depth" : 25 * mm, "endBoundEntityFace" : qUnion([Q1]), "offsetDistance" : 25 * mm});
        }
        {
            var Q0;
            {var subQ0=makeQuery(id+"F9.opExtrude","CAP_FACE",FACE,{"disambiguationData":[OSD([sQuery(id+"F8.wireOp",EDGE,"E8.0.0"),sQuery(id+"F8.wireOp",EDGE,"E8.0.1"),sQuery(id+"F8.wireOp",EDGE,"E8.0.2"),sQuery(id+"F8.wireOp",EDGE,"E8.0.3"),sQuery(id+"F8.wireOp",EDGE,"E8.0.4"),sQuery(id+"F8.wireOp",EDGE,"E8.0.5"),sQuery(id+"F8.wireOp",EDGE,"E8.0.6"),sQuery(id+"F8.wireOp",EDGE,"E8.0.7"),sQuery(id+"F8.wireOp",EDGE,"E9.0.0"),sQuery(id+"F8.wireOp",EDGE,"E9.0.1"),sQuery(id+"F8.wireOp",EDGE,"E9.0.2"),sQuery(id+"F8.wireOp",EDGE,"E9.0.3"),sQuery(id+"F8.wireOp",EDGE,"E9.0.4"),sQuery(id+"F8.wireOp",EDGE,"E9.0.5"),sQuery(id+"F8.wireOp",EDGE,"E9.0.6"),sQuery(id+"F8.wireOp",EDGE,"E9.0.7")])],"isStart":false});var subQ1=sQuery(id+"F0.wireOp",EDGE,"E0.right");var subQ2=makeQuery(id+"F6.opExtrude","CAP_FACE",FACE,{"disambiguationData":[OSD([sQuery(id+"F5.wireOp",EDGE,"E6.0.0"),sQuery(id+"F5.wireOp",EDGE,"E6.0.1"),sQuery(id+"F5.wireOp",EDGE,"E6.0.2"),sQuery(id+"F5.wireOp",EDGE,"E6.0.3"),sQuery(id+"F5.wireOp",EDGE,"E6.0.4"),sQuery(id+"F5.wireOp",EDGE,"E6.0.5"),sQuery(id+"F5.wireOp",EDGE,"E6.0.6"),sQuery(id+"F5.wireOp",EDGE,"E6.0.7"),sQuery(id+"F5.wireOp",EDGE,"E7.0.0"),sQuery(id+"F5.wireOp",EDGE,"E7.0.1"),sQuery(id+"F5.wireOp",EDGE,"E7.0.2"),sQuery(id+"F5.wireOp",EDGE,"E7.0.3"),sQuery(id+"F5.wireOp",EDGE,"E7.0.4"),sQuery(id+"F5.wireOp",EDGE,"E7.0.5"),sQuery(id+"F5.wireOp",EDGE,"E7.0.6"),sQuery(id+"F5.wireOp",EDGE,"E7.0.7")])],"isStart":true});var subQ3=makeQuery(id+"F19.opPattern","COPY",FACE,{"derivedFrom":makeQuery(id+"F16.boolean.opBoolean","SPLIT",FACE,{"disambiguationData":[TD([subQ2])],"derivedFrom":makeQuery(id+"F16.opExtrude","SWEPT_FACE",FACE,{"disambiguationData":[OSD([sQuery(id+"F15.wireOp",EDGE,"E17.top")])]})}),"instanceName":"1"});var subQ4=makeQuery(id+"F21.opPattern","COPY",FACE,{"derivedFrom":subQ3,"instanceName":"1"});var subQ5=sQuery(id+"F0.wireOp",EDGE,"E0.left");var subQ6=makeQuery(id+"F1.opExtrude","SWEPT_FACE",FACE,{"disambiguationData":[OSD([subQ5])]});var subQ7=sQuery(id+"F0.wireOp",EDGE,"E2.filletArc");var subQ8=makeQuery(id+"F1.opExtrude","SWEPT_FACE",FACE,{"disambiguationData":[OSD([subQ7])]});var subQ9=sQuery(id+"F0.wireOp",EDGE,"E3.filletArc");Q0=makeQuery(id+"F29.boolean.opBoolean","SPLIT",FACE,{"disambiguationData":[TD([makeQuery(id+"F29.opExtrude","SWEPT_FACE",FACE,{"disambiguationData":[OSD([sQuery(id+"F28.wireOp",EDGE,"E397.top")])]})])],"derivedFrom":makeQuery(id+"F27.boolean.opBoolean","SPLIT",FACE,{"disambiguationData":[TD([subQ6,subQ0,subQ3,subQ4,makeQuery(id+"F27.opExtrude","SWEPT_FACE",FACE,{"disambiguationData":[OSD([sQuery(id+"F26.wireOp",EDGE,"E394.top")])]}),makeQuery(id+"F27.opExtrude","SWEPT_FACE",FACE,{"disambiguationData":[OSD([sQuery(id+"F26.wireOp",EDGE,"E395")])]}),makeQuery(id+"F27.opExtrude","SWEPT_FACE",FACE,{"disambiguationData":[OSD([sQuery(id+"F26.wireOp",EDGE,"E396")])]})])],"derivedFrom":makeQuery(id+"F21.boolean.opBoolean","SPLIT",FACE,{"disambiguationData":[TD([subQ3])],"derivedFrom":makeQuery(id+"F19.boolean.opBoolean","SPLIT",FACE,{"disambiguationData":[TD([subQ8])],"derivedFrom":makeQuery(id+"F9.boolean.opBoolean","SPLIT",FACE,{"disambiguationData":[TD([subQ2])],"derivedFrom":makeQuery(id+"F6.boolean.opBoolean","SPLIT",FACE,{"disambiguationData":[TD([makeQuery(id+"F1.opExtrude","CAP_FACE",FACE,{"disambiguationData":[OSD([sQuery(id+"F0.wireOp",EDGE,"E0.bottom"),sQuery(id+"F0.wireOp",EDGE,"E0.top"),subQ5,subQ1,sQuery(id+"F0.wireOp",EDGE,"E1.filletArc"),subQ7,subQ9,sQuery(id+"F0.wireOp",EDGE,"E4.filletArc")])],"isStart":true})])],"derivedFrom":subQ6})})})})})});}
            var sketch = newSketch(context, id + "F30", { "sketchPlane" : qUnion([Q0])});
            skArc(sketch, "E398.0", {"start": v(66, 78) * mm, "mid": v(61.02, 90.02) * mm, "end": v(49, 95) * mm});
            skArc(sketch, "E399.0", {"start": v(49, 61) * mm, "mid": v(61.02, 65.98) * mm, "end": v(66, 78) * mm});
            skLineSegment(sketch, "E400.0", {"start": v(-66, 61) * mm, "end": v(-49, 61) * mm});
            skLineSegment(sketch, "E401.0", {"start": v(66, 95) * mm, "end": v(66, 61) * mm});
            skLineSegment(sketch, "E402.0", {"start": v(66, 95) * mm, "end": v(49, 95) * mm});
            skArc(sketch, "E403.0", {"start": v(-66, 78) * mm, "mid": v(-61.02, 65.98) * mm, "end": v(-49, 61) * mm});
            skArc(sketch, "E404.0", {"start": v(-49, 95) * mm, "mid": v(-61.02, 90.02) * mm, "end": v(-66, 78) * mm});
            skLineSegment(sketch, "E405.0", {"start": v(-66, 95) * mm, "end": v(-66, 61) * mm});
            skLineSegment(sketch, "E406.trimOffspring", {"start": v(-49, 95) * mm, "end": v(-149, 95) * mm});
            skLineSegment(sketch, "E407.trimOffspring", {"start": v(49, 61) * mm, "end": v(66, 61) * mm});
            skPoint(sketch, "E408.orphan", {"position": v(149, 95) * mm});
            skSolve(sketch);
        }
        {
            var Q0;
            Q0 = qSketchRegion(id + "F30", true);
            var Q1;
            {var subQ0=makeQuery(id+"F20.opPattern","COPY",FACE,{"derivedFrom":makeQuery(id+"F16.boolean.opBoolean","SPLIT",FACE,{"disambiguationData":[TD([makeQuery(id+"F6.opExtrude","CAP_FACE",FACE,{"disambiguationData":[OSD([sQuery(id+"F5.wireOp",EDGE,"E6.0.0"),sQuery(id+"F5.wireOp",EDGE,"E6.0.1"),sQuery(id+"F5.wireOp",EDGE,"E6.0.2"),sQuery(id+"F5.wireOp",EDGE,"E6.0.3"),sQuery(id+"F5.wireOp",EDGE,"E6.0.4"),sQuery(id+"F5.wireOp",EDGE,"E6.0.5"),sQuery(id+"F5.wireOp",EDGE,"E6.0.6"),sQuery(id+"F5.wireOp",EDGE,"E6.0.7"),sQuery(id+"F5.wireOp",EDGE,"E7.0.0"),sQuery(id+"F5.wireOp",EDGE,"E7.0.1"),sQuery(id+"F5.wireOp",EDGE,"E7.0.2"),sQuery(id+"F5.wireOp",EDGE,"E7.0.3"),sQuery(id+"F5.wireOp",EDGE,"E7.0.4"),sQuery(id+"F5.wireOp",EDGE,"E7.0.5"),sQuery(id+"F5.wireOp",EDGE,"E7.0.6"),sQuery(id+"F5.wireOp",EDGE,"E7.0.7")])],"isStart":true})])],"derivedFrom":makeQuery(id+"F16.opExtrude","SWEPT_FACE",FACE,{"disambiguationData":[OSD([sQuery(id+"F15.wireOp",EDGE,"E17.right")])]})}),"instanceName":"1"});Q1=makeQuery(id+"F29.boolean.opBoolean","MERGE",FACE,{"derivedFrom":[subQ0,makeQuery(id+"F21.opPattern","COPY",FACE,{"derivedFrom":subQ0,"instanceName":"1"}),makeQuery(id+"F29.opExtrude","CAP_FACE",FACE,{"disambiguationData":[OSD([sQuery(id+"F28.wireOp",EDGE,"E397.bottom"),sQuery(id+"F28.wireOp",EDGE,"E397.top"),sQuery(id+"F28.wireOp",EDGE,"E397.left"),sQuery(id+"F28.wireOp",EDGE,"E397.right")])],"isStart":false})]});}
            extrude(context, id + "F31", {"entities" : qUnion([Q0]), "operationType" : NewBodyOperationType.ADD, "endBound" : BoundingType.UP_TO_SURFACE, "depth" : 25 * mm, "endBoundEntityFace" : qUnion([Q1]), "offsetDistance" : 25 * mm});
        }
        {
            var Q0;
            Q0=makeQuery(id+"F1.opExtrude","SWEPT_BODY",BODY,{"disambiguationData":[OSD([sQuery(id+"F0.wireOp",EDGE,"E0.bottom"),sQuery(id+"F0.wireOp",EDGE,"E0.top"),sQuery(id+"F0.wireOp",EDGE,"E0.left"),sQuery(id+"F0.wireOp",EDGE,"E0.right"),sQuery(id+"F0.wireOp",EDGE,"E1.filletArc"),sQuery(id+"F0.wireOp",EDGE,"E2.filletArc"),sQuery(id+"F0.wireOp",EDGE,"E3.filletArc"),sQuery(id+"F0.wireOp",EDGE,"E4.filletArc")])]});
            var Q1;
            Q1=qCreatedBy(makeId("Right.planeOp"),FACE);
            mirror(context, id + "F32", {"operationType" : NewBodyOperationType.ADD, "entities" : qUnion([Q0]), "mirrorPlane" : qUnion([Q1])});
        }
    });
